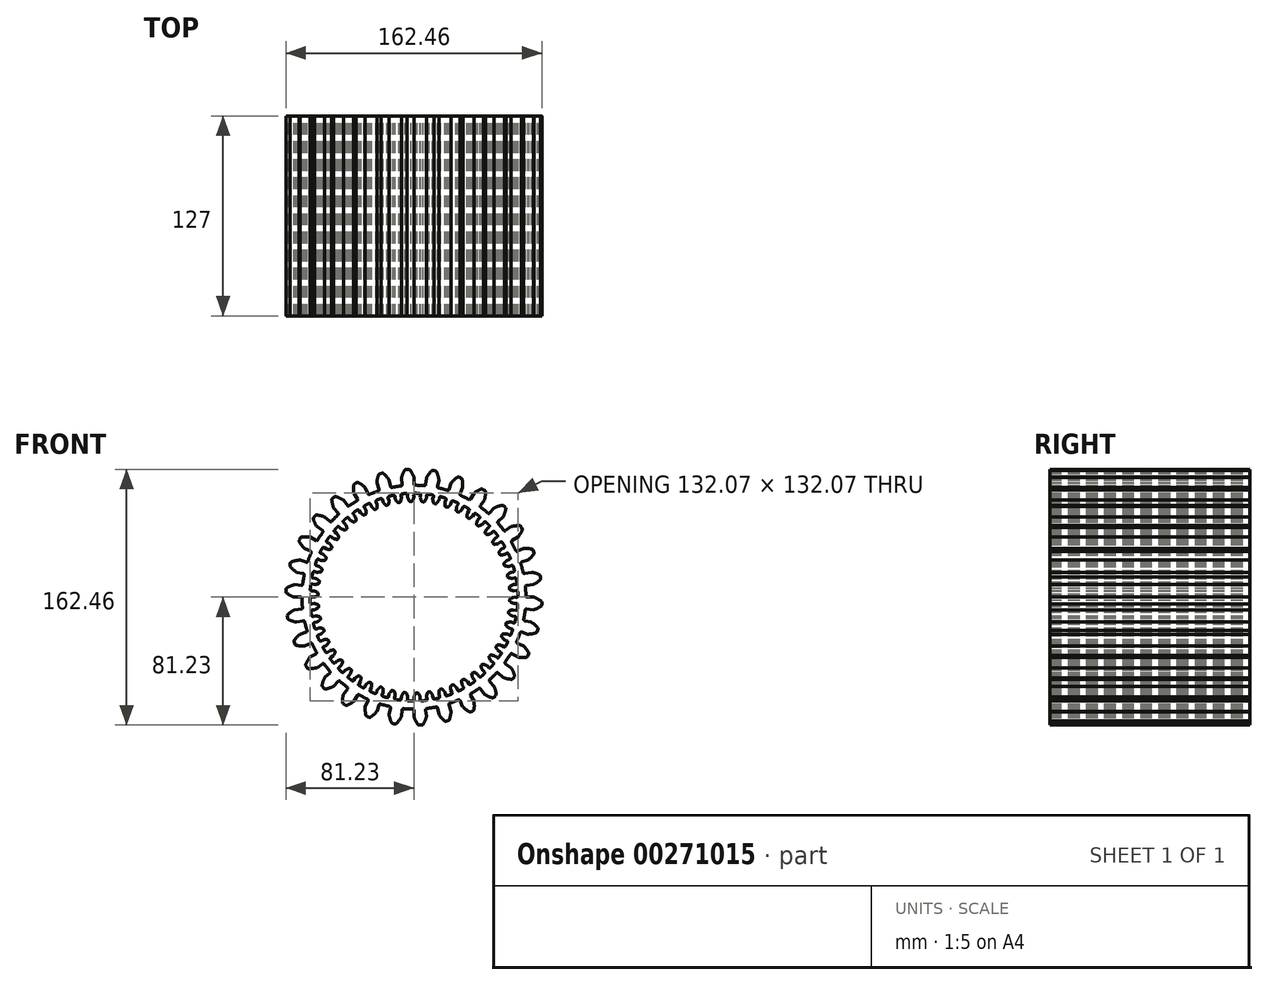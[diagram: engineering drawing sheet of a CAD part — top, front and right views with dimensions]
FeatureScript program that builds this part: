
annotation { "Feature Type Name" : "Feature", "Feature Type Description" : "" }
export const myFeature = defineFeature(function(context is Context, id is Id, definition is map)
    precondition{}
    {
        {
            var Q0;
            Q0=qCreatedBy(makeId("Front.planeOp"),FACE);
            var sketch = newSketch(context, id + "F0", { "sketchPlane" : qUnion([Q0])});
            skArc(sketch, "E0", {"start": v(-8.2, 70.64) * mm, "mid": v(-11.13, 70.24) * mm, "end": v(-14.02, 69.72) * mm});
            skLineSegment(sketch, "E1", {"start": v(-3.26, 81.23) * mm, "end": v(-4.26, 81.23) * mm});
            skLineSegment(sketch, "E2", {"start": v(0, 76.2) * mm, "end": v(0, 71.9) * mm});
            skArc(sketch, "E3.trimOffspring", {"start": v(0, 76.2) * mm, "mid": v(-1.15, 78.65) * mm, "end": v(-2.64, 80.92) * mm});
            skLineSegment(sketch, "E4.MirrorCS", {"start": v(-5.25, 81.13) * mm, "end": v(-4.26, 81.23) * mm});
            skArc(sketch, "E5.MirrorCS", {"start": v(-7.97, 75.78) * mm, "mid": v(-7.08, 78.34) * mm, "end": v(-5.84, 80.75) * mm});
            skLineSegment(sketch, "E6.MirrorCS", {"start": v(-7.97, 75.78) * mm, "end": v(-7.52, 71.5) * mm});
            skPoint(sketch, "E7.visualSharp", {"position": v(-5.63, 81.08) * mm});
            skArc(sketch, "E7.filletArc", {"start": v(-5.25, 81.13) * mm, "mid": v(-5.58, 81) * mm, "end": v(-5.84, 80.75) * mm});
            skPoint(sketch, "E8.visualSharp", {"position": v(-2.88, 81.23) * mm});
            skArc(sketch, "E8.filletArc", {"start": v(-2.64, 80.92) * mm, "mid": v(-2.91, 81.15) * mm, "end": v(-3.26, 81.23) * mm});
            skPoint(sketch, "E9.visualSharp", {"position": v(-7.43, 70.73) * mm});
            skArc(sketch, "E9.filletArc", {"start": v(-8.2, 70.64) * mm, "mid": v(-7.68, 70.93) * mm, "end": v(-7.52, 71.5) * mm});
            skPoint(sketch, "E10.visualSharp", {"position": v(0, 71.12) * mm});
            skArc(sketch, "E10.filletArc", {"start": v(0, 71.9) * mm, "mid": v(0.23, 71.35) * mm, "end": v(0.78, 71.12) * mm});
            skLineSegment(sketch, "E11.1.0", {"start": v(-22, 78.26) * mm, "end": v(-21.05, 78.57) * mm});
            skArc(sketch, "E11.1.1", {"start": v(-22, 78.26) * mm, "mid": v(-22.3, 78.08) * mm, "end": v(-22.5, 77.77) * mm});
            skArc(sketch, "E11.1.2", {"start": v(-23.55, 72.47) * mm, "mid": v(-23.21, 75.16) * mm, "end": v(-22.5, 77.77) * mm});
            skLineSegment(sketch, "E11.1.3", {"start": v(-23.55, 72.47) * mm, "end": v(-22.22, 68.38) * mm});
            skArc(sketch, "E11.1.4", {"start": v(-22.72, 67.4) * mm, "mid": v(-22.26, 67.79) * mm, "end": v(-22.22, 68.38) * mm});
            skLineSegment(sketch, "E11.1.5", {"start": v(-20.08, 78.78) * mm, "end": v(-21.05, 78.57) * mm});
            skArc(sketch, "E11.1.6", {"start": v(-19.4, 78.6) * mm, "mid": v(-19.72, 78.77) * mm, "end": v(-20.08, 78.78) * mm});
            skArc(sketch, "E11.1.7", {"start": v(-15.84, 74.53) * mm, "mid": v(-17.48, 76.7) * mm, "end": v(-19.4, 78.6) * mm});
            skLineSegment(sketch, "E11.1.8", {"start": v(-15.84, 74.53) * mm, "end": v(-14.95, 70.33) * mm});
            skArc(sketch, "E11.1.9", {"start": v(-14.95, 70.33) * mm, "mid": v(-14.61, 69.84) * mm, "end": v(-14.02, 69.72) * mm});
            skLineSegment(sketch, "E11.2.0", {"start": v(-37.79, 71.98) * mm, "end": v(-36.93, 72.47) * mm});
            skArc(sketch, "E11.2.1", {"start": v(-37.79, 71.98) * mm, "mid": v(-38.05, 71.73) * mm, "end": v(-38.18, 71.4) * mm});
            skArc(sketch, "E11.2.2", {"start": v(-38.1, 66) * mm, "mid": v(-38.33, 68.7) * mm, "end": v(-38.18, 71.4) * mm});
            skLineSegment(sketch, "E11.2.3", {"start": v(-38.1, 66) * mm, "end": v(-35.95, 62.27) * mm});
            skArc(sketch, "E11.2.4", {"start": v(-36.23, 61.2) * mm, "mid": v(-35.87, 61.68) * mm, "end": v(-35.95, 62.27) * mm});
            skLineSegment(sketch, "E11.2.5", {"start": v(-36.02, 72.88) * mm, "end": v(-36.93, 72.47) * mm});
            skArc(sketch, "E11.2.6", {"start": v(-35.32, 72.85) * mm, "mid": v(-35.67, 72.95) * mm, "end": v(-36.02, 72.88) * mm});
            skArc(sketch, "E11.2.7", {"start": v(-31, 69.61) * mm, "mid": v(-33.04, 71.39) * mm, "end": v(-35.32, 72.85) * mm});
            skLineSegment(sketch, "E11.2.8", {"start": v(-31, 69.61) * mm, "end": v(-29.25, 65.69) * mm});
            skArc(sketch, "E11.2.9", {"start": v(-29.25, 65.69) * mm, "mid": v(-28.81, 65.27) * mm, "end": v(-28.21, 65.28) * mm});
            skLineSegment(sketch, "E11.3.0", {"start": v(-51.93, 62.55) * mm, "end": v(-51.19, 63.21) * mm});
            skArc(sketch, "E11.3.1", {"start": v(-51.93, 62.55) * mm, "mid": v(-52.13, 62.25) * mm, "end": v(-52.19, 61.9) * mm});
            skArc(sketch, "E11.3.2", {"start": v(-50.99, 56.63) * mm, "mid": v(-51.77, 59.22) * mm, "end": v(-52.19, 61.9) * mm});
            skLineSegment(sketch, "E11.3.3", {"start": v(-50.99, 56.63) * mm, "end": v(-48.11, 53.43) * mm});
            skArc(sketch, "E11.3.4", {"start": v(-48.16, 52.33) * mm, "mid": v(-47.91, 52.87) * mm, "end": v(-48.11, 53.43) * mm});
            skLineSegment(sketch, "E11.3.5", {"start": v(-50.38, 63.8) * mm, "end": v(-51.19, 63.21) * mm});
            skArc(sketch, "E11.3.6", {"start": v(-49.7, 63.92) * mm, "mid": v(-50.05, 63.94) * mm, "end": v(-50.38, 63.8) * mm});
            skArc(sketch, "E11.3.7", {"start": v(-44.79, 61.65) * mm, "mid": v(-47.16, 62.96) * mm, "end": v(-49.7, 63.92) * mm});
            skLineSegment(sketch, "E11.3.8", {"start": v(-44.79, 61.65) * mm, "end": v(-42.26, 58.17) * mm});
            skArc(sketch, "E11.3.9", {"start": v(-42.26, 58.17) * mm, "mid": v(-41.75, 57.86) * mm, "end": v(-41.17, 58) * mm});
            skLineSegment(sketch, "E11.4.0", {"start": v(-63.8, 50.38) * mm, "end": v(-63.21, 51.19) * mm});
            skArc(sketch, "E11.4.1", {"start": v(-63.8, 50.38) * mm, "mid": v(-63.94, 50.05) * mm, "end": v(-63.92, 49.7) * mm});
            skArc(sketch, "E11.4.2", {"start": v(-61.65, 44.79) * mm, "mid": v(-62.96, 47.16) * mm, "end": v(-63.92, 49.7) * mm});
            skLineSegment(sketch, "E11.4.3", {"start": v(-61.65, 44.79) * mm, "end": v(-58.17, 42.26) * mm});
            skArc(sketch, "E11.4.4", {"start": v(-58, 41.17) * mm, "mid": v(-57.86, 41.75) * mm, "end": v(-58.17, 42.26) * mm});
            skLineSegment(sketch, "E11.4.5", {"start": v(-62.55, 51.93) * mm, "end": v(-63.21, 51.19) * mm});
            skArc(sketch, "E11.4.6", {"start": v(-61.9, 52.19) * mm, "mid": v(-62.25, 52.13) * mm, "end": v(-62.55, 51.93) * mm});
            skArc(sketch, "E11.4.7", {"start": v(-56.63, 50.99) * mm, "mid": v(-59.22, 51.77) * mm, "end": v(-61.9, 52.19) * mm});
            skLineSegment(sketch, "E11.4.8", {"start": v(-56.63, 50.99) * mm, "end": v(-53.43, 48.11) * mm});
            skArc(sketch, "E11.4.9", {"start": v(-53.43, 48.11) * mm, "mid": v(-52.87, 47.91) * mm, "end": v(-52.33, 48.16) * mm});
            skLineSegment(sketch, "E11.5.0", {"start": v(-72.88, 36.02) * mm, "end": v(-72.47, 36.93) * mm});
            skArc(sketch, "E11.5.1", {"start": v(-72.88, 36.02) * mm, "mid": v(-72.95, 35.67) * mm, "end": v(-72.85, 35.32) * mm});
            skArc(sketch, "E11.5.2", {"start": v(-69.61, 31) * mm, "mid": v(-71.39, 33.04) * mm, "end": v(-72.85, 35.32) * mm});
            skLineSegment(sketch, "E11.5.3", {"start": v(-69.61, 31) * mm, "end": v(-65.69, 29.25) * mm});
            skArc(sketch, "E11.5.4", {"start": v(-65.28, 28.21) * mm, "mid": v(-65.27, 28.81) * mm, "end": v(-65.69, 29.25) * mm});
            skLineSegment(sketch, "E11.5.5", {"start": v(-71.98, 37.79) * mm, "end": v(-72.47, 36.93) * mm});
            skArc(sketch, "E11.5.6", {"start": v(-71.4, 38.18) * mm, "mid": v(-71.73, 38.05) * mm, "end": v(-71.98, 37.79) * mm});
            skArc(sketch, "E11.5.7", {"start": v(-66, 38.1) * mm, "mid": v(-68.7, 38.33) * mm, "end": v(-71.4, 38.18) * mm});
            skLineSegment(sketch, "E11.5.8", {"start": v(-66, 38.1) * mm, "end": v(-62.27, 35.95) * mm});
            skArc(sketch, "E11.5.9", {"start": v(-62.27, 35.95) * mm, "mid": v(-61.68, 35.87) * mm, "end": v(-61.2, 36.23) * mm});
            skLineSegment(sketch, "E11.6.0", {"start": v(-78.78, 20.08) * mm, "end": v(-78.57, 21.05) * mm});
            skArc(sketch, "E11.6.1", {"start": v(-78.78, 20.08) * mm, "mid": v(-78.77, 19.72) * mm, "end": v(-78.6, 19.4) * mm});
            skArc(sketch, "E11.6.2", {"start": v(-74.53, 15.84) * mm, "mid": v(-76.7, 17.48) * mm, "end": v(-78.6, 19.4) * mm});
            skLineSegment(sketch, "E11.6.3", {"start": v(-74.53, 15.84) * mm, "end": v(-70.33, 14.95) * mm});
            skArc(sketch, "E11.6.4", {"start": v(-69.72, 14.02) * mm, "mid": v(-69.84, 14.61) * mm, "end": v(-70.33, 14.95) * mm});
            skLineSegment(sketch, "E11.6.5", {"start": v(-78.26, 22) * mm, "end": v(-78.57, 21.05) * mm});
            skArc(sketch, "E11.6.6", {"start": v(-77.77, 22.5) * mm, "mid": v(-78.08, 22.3) * mm, "end": v(-78.26, 22) * mm});
            skArc(sketch, "E11.6.7", {"start": v(-72.47, 23.55) * mm, "mid": v(-75.16, 23.21) * mm, "end": v(-77.77, 22.5) * mm});
            skLineSegment(sketch, "E11.6.8", {"start": v(-72.47, 23.55) * mm, "end": v(-68.38, 22.22) * mm});
            skArc(sketch, "E11.6.9", {"start": v(-68.38, 22.22) * mm, "mid": v(-67.79, 22.26) * mm, "end": v(-67.4, 22.72) * mm});
            skLineSegment(sketch, "E11.7.0", {"start": v(-81.23, 3.26) * mm, "end": v(-81.23, 4.26) * mm});
            skArc(sketch, "E11.7.1", {"start": v(-81.23, 3.26) * mm, "mid": v(-81.15, 2.91) * mm, "end": v(-80.92, 2.64) * mm});
            skArc(sketch, "E11.7.2", {"start": v(-76.2, 0) * mm, "mid": v(-78.65, 1.15) * mm, "end": v(-80.92, 2.64) * mm});
            skLineSegment(sketch, "E11.7.3", {"start": v(-76.2, 0) * mm, "end": v(-71.9, 0) * mm});
            skArc(sketch, "E11.7.4", {"start": v(-71.12, -0.78) * mm, "mid": v(-71.35, -0.23) * mm, "end": v(-71.9, 0) * mm});
            skLineSegment(sketch, "E11.7.5", {"start": v(-81.13, 5.25) * mm, "end": v(-81.23, 4.26) * mm});
            skArc(sketch, "E11.7.6", {"start": v(-80.75, 5.84) * mm, "mid": v(-81, 5.58) * mm, "end": v(-81.13, 5.25) * mm});
            skArc(sketch, "E11.7.7", {"start": v(-75.78, 7.97) * mm, "mid": v(-78.34, 7.08) * mm, "end": v(-80.75, 5.84) * mm});
            skLineSegment(sketch, "E11.7.8", {"start": v(-75.78, 7.97) * mm, "end": v(-71.5, 7.52) * mm});
            skArc(sketch, "E11.7.9", {"start": v(-71.5, 7.52) * mm, "mid": v(-70.93, 7.68) * mm, "end": v(-70.64, 8.2) * mm});
            skLineSegment(sketch, "E11.8.0", {"start": v(-80.13, -13.7) * mm, "end": v(-80.34, -12.72) * mm});
            skArc(sketch, "E11.8.1", {"start": v(-80.13, -13.7) * mm, "mid": v(-79.98, -14.02) * mm, "end": v(-79.7, -14.24) * mm});
            skArc(sketch, "E11.8.2", {"start": v(-74.53, -15.84) * mm, "mid": v(-77.17, -15.23) * mm, "end": v(-79.7, -14.24) * mm});
            skLineSegment(sketch, "E11.8.3", {"start": v(-74.53, -15.84) * mm, "end": v(-70.33, -14.95) * mm});
            skArc(sketch, "E11.8.4", {"start": v(-69.4, -15.55) * mm, "mid": v(-69.74, -15.06) * mm, "end": v(-70.33, -14.95) * mm});
            skLineSegment(sketch, "E11.8.5", {"start": v(-80.44, -11.74) * mm, "end": v(-80.34, -12.72) * mm});
            skArc(sketch, "E11.8.6", {"start": v(-80.2, -11.08) * mm, "mid": v(-80.4, -11.38) * mm, "end": v(-80.44, -11.74) * mm});
            skArc(sketch, "E11.8.7", {"start": v(-75.78, -7.97) * mm, "mid": v(-78.1, -9.37) * mm, "end": v(-80.2, -11.08) * mm});
            skLineSegment(sketch, "E11.8.8", {"start": v(-75.78, -7.97) * mm, "end": v(-71.5, -7.52) * mm});
            skArc(sketch, "E11.8.9", {"start": v(-71.5, -7.52) * mm, "mid": v(-70.98, -7.23) * mm, "end": v(-70.8, -6.66) * mm});
            skLineSegment(sketch, "E11.9.0", {"start": v(-75.53, -30.06) * mm, "end": v(-75.94, -29.15) * mm});
            skArc(sketch, "E11.9.1", {"start": v(-75.53, -30.06) * mm, "mid": v(-75.32, -30.34) * mm, "end": v(-75, -30.5) * mm});
            skArc(sketch, "E11.9.2", {"start": v(-69.61, -31) * mm, "mid": v(-72.32, -30.94) * mm, "end": v(-75, -30.5) * mm});
            skLineSegment(sketch, "E11.9.3", {"start": v(-69.61, -31) * mm, "end": v(-65.69, -29.25) * mm});
            skArc(sketch, "E11.9.4", {"start": v(-64.65, -29.64) * mm, "mid": v(-65.09, -29.23) * mm, "end": v(-65.69, -29.25) * mm});
            skLineSegment(sketch, "E11.9.5", {"start": v(-76.25, -28.2) * mm, "end": v(-75.94, -29.15) * mm});
            skArc(sketch, "E11.9.6", {"start": v(-76.14, -27.51) * mm, "mid": v(-76.28, -27.85) * mm, "end": v(-76.25, -28.2) * mm});
            skArc(sketch, "E11.9.7", {"start": v(-72.47, -23.55) * mm, "mid": v(-74.45, -25.4) * mm, "end": v(-76.14, -27.51) * mm});
            skLineSegment(sketch, "E11.9.8", {"start": v(-72.47, -23.55) * mm, "end": v(-68.38, -22.22) * mm});
            skArc(sketch, "E11.9.9", {"start": v(-68.38, -22.22) * mm, "mid": v(-67.93, -21.83) * mm, "end": v(-67.88, -21.24) * mm});
            skLineSegment(sketch, "E11.10.0", {"start": v(-67.63, -45.1) * mm, "end": v(-68.22, -44.3) * mm});
            skArc(sketch, "E11.10.1", {"start": v(-67.63, -45.1) * mm, "mid": v(-67.36, -45.34) * mm, "end": v(-67.01, -45.43) * mm});
            skArc(sketch, "E11.10.2", {"start": v(-61.65, -44.79) * mm, "mid": v(-64.3, -45.3) * mm, "end": v(-67.01, -45.43) * mm});
            skLineSegment(sketch, "E11.10.3", {"start": v(-61.65, -44.79) * mm, "end": v(-58.17, -42.26) * mm});
            skArc(sketch, "E11.10.4", {"start": v(-57.08, -42.43) * mm, "mid": v(-57.59, -42.12) * mm, "end": v(-58.17, -42.26) * mm});
            skLineSegment(sketch, "E11.10.5", {"start": v(-68.72, -43.44) * mm, "end": v(-68.22, -44.3) * mm});
            skArc(sketch, "E11.10.6", {"start": v(-68.76, -42.74) * mm, "mid": v(-68.82, -43.1) * mm, "end": v(-68.72, -43.44) * mm});
            skArc(sketch, "E11.10.7", {"start": v(-66, -38.1) * mm, "mid": v(-67.54, -40.32) * mm, "end": v(-68.76, -42.74) * mm});
            skLineSegment(sketch, "E11.10.8", {"start": v(-66, -38.1) * mm, "end": v(-62.27, -35.95) * mm});
            skArc(sketch, "E11.10.9", {"start": v(-62.27, -35.95) * mm, "mid": v(-61.9, -35.48) * mm, "end": v(-61.98, -34.88) * mm});
            skLineSegment(sketch, "E11.11.0", {"start": v(-56.78, -58.18) * mm, "end": v(-57.52, -57.52) * mm});
            skArc(sketch, "E11.11.1", {"start": v(-56.78, -58.18) * mm, "mid": v(-56.46, -58.35) * mm, "end": v(-56.1, -58.37) * mm});
            skArc(sketch, "E11.11.2", {"start": v(-50.99, -56.63) * mm, "mid": v(-53.48, -57.68) * mm, "end": v(-56.1, -58.37) * mm});
            skLineSegment(sketch, "E11.11.3", {"start": v(-50.99, -56.63) * mm, "end": v(-48.11, -53.43) * mm});
            skArc(sketch, "E11.11.4", {"start": v(-47, -53.37) * mm, "mid": v(-47.57, -53.18) * mm, "end": v(-48.11, -53.43) * mm});
            skLineSegment(sketch, "E11.11.5", {"start": v(-58.18, -56.78) * mm, "end": v(-57.52, -57.52) * mm});
            skArc(sketch, "E11.11.6", {"start": v(-58.37, -56.1) * mm, "mid": v(-58.35, -56.46) * mm, "end": v(-58.18, -56.78) * mm});
            skArc(sketch, "E11.11.7", {"start": v(-56.63, -50.99) * mm, "mid": v(-57.68, -53.48) * mm, "end": v(-58.37, -56.1) * mm});
            skLineSegment(sketch, "E11.11.8", {"start": v(-56.63, -50.99) * mm, "end": v(-53.43, -48.11) * mm});
            skArc(sketch, "E11.11.9", {"start": v(-53.43, -48.11) * mm, "mid": v(-53.18, -47.57) * mm, "end": v(-53.37, -47) * mm});
            skLineSegment(sketch, "E11.12.0", {"start": v(-43.44, -68.72) * mm, "end": v(-44.3, -68.22) * mm});
            skArc(sketch, "E11.12.1", {"start": v(-43.44, -68.72) * mm, "mid": v(-43.1, -68.82) * mm, "end": v(-42.74, -68.76) * mm});
            skArc(sketch, "E11.12.2", {"start": v(-38.1, -66) * mm, "mid": v(-40.32, -67.54) * mm, "end": v(-42.74, -68.76) * mm});
            skLineSegment(sketch, "E11.12.3", {"start": v(-38.1, -66) * mm, "end": v(-35.95, -62.27) * mm});
            skArc(sketch, "E11.12.4", {"start": v(-34.88, -61.98) * mm, "mid": v(-35.48, -61.9) * mm, "end": v(-35.95, -62.27) * mm});
            skLineSegment(sketch, "E11.12.5", {"start": v(-45.1, -67.63) * mm, "end": v(-44.3, -68.22) * mm});
            skArc(sketch, "E11.12.6", {"start": v(-45.43, -67.01) * mm, "mid": v(-45.34, -67.36) * mm, "end": v(-45.1, -67.63) * mm});
            skArc(sketch, "E11.12.7", {"start": v(-44.79, -61.65) * mm, "mid": v(-45.3, -64.3) * mm, "end": v(-45.43, -67.01) * mm});
            skLineSegment(sketch, "E11.12.8", {"start": v(-44.79, -61.65) * mm, "end": v(-42.26, -58.17) * mm});
            skArc(sketch, "E11.12.9", {"start": v(-42.26, -58.17) * mm, "mid": v(-42.12, -57.59) * mm, "end": v(-42.43, -57.08) * mm});
            skLineSegment(sketch, "E11.13.0", {"start": v(-28.2, -76.25) * mm, "end": v(-29.15, -75.94) * mm});
            skArc(sketch, "E11.13.1", {"start": v(-28.2, -76.25) * mm, "mid": v(-27.85, -76.28) * mm, "end": v(-27.51, -76.14) * mm});
            skArc(sketch, "E11.13.2", {"start": v(-23.55, -72.47) * mm, "mid": v(-25.4, -74.45) * mm, "end": v(-27.51, -76.14) * mm});
            skLineSegment(sketch, "E11.13.3", {"start": v(-23.55, -72.47) * mm, "end": v(-22.22, -68.38) * mm});
            skArc(sketch, "E11.13.4", {"start": v(-21.24, -67.88) * mm, "mid": v(-21.83, -67.93) * mm, "end": v(-22.22, -68.38) * mm});
            skLineSegment(sketch, "E11.13.5", {"start": v(-30.06, -75.53) * mm, "end": v(-29.15, -75.94) * mm});
            skArc(sketch, "E11.13.6", {"start": v(-30.5, -75) * mm, "mid": v(-30.34, -75.32) * mm, "end": v(-30.06, -75.53) * mm});
            skArc(sketch, "E11.13.7", {"start": v(-31, -69.61) * mm, "mid": v(-30.94, -72.32) * mm, "end": v(-30.5, -75) * mm});
            skLineSegment(sketch, "E11.13.8", {"start": v(-31, -69.61) * mm, "end": v(-29.25, -65.69) * mm});
            skArc(sketch, "E11.13.9", {"start": v(-29.25, -65.69) * mm, "mid": v(-29.23, -65.09) * mm, "end": v(-29.64, -64.65) * mm});
            skLineSegment(sketch, "E11.14.0", {"start": v(-11.74, -80.44) * mm, "end": v(-12.72, -80.34) * mm});
            skArc(sketch, "E11.14.1", {"start": v(-11.74, -80.44) * mm, "mid": v(-11.38, -80.4) * mm, "end": v(-11.08, -80.2) * mm});
            skArc(sketch, "E11.14.2", {"start": v(-7.97, -75.78) * mm, "mid": v(-9.37, -78.1) * mm, "end": v(-11.08, -80.2) * mm});
            skLineSegment(sketch, "E11.14.3", {"start": v(-7.97, -75.78) * mm, "end": v(-7.52, -71.5) * mm});
            skArc(sketch, "E11.14.4", {"start": v(-6.66, -70.8) * mm, "mid": v(-7.23, -70.98) * mm, "end": v(-7.52, -71.5) * mm});
            skLineSegment(sketch, "E11.14.5", {"start": v(-13.7, -80.13) * mm, "end": v(-12.72, -80.34) * mm});
            skArc(sketch, "E11.14.6", {"start": v(-14.24, -79.7) * mm, "mid": v(-14.02, -79.98) * mm, "end": v(-13.7, -80.13) * mm});
            skArc(sketch, "E11.14.7", {"start": v(-15.84, -74.53) * mm, "mid": v(-15.23, -77.17) * mm, "end": v(-14.24, -79.7) * mm});
            skLineSegment(sketch, "E11.14.8", {"start": v(-15.84, -74.53) * mm, "end": v(-14.95, -70.33) * mm});
            skArc(sketch, "E11.14.9", {"start": v(-14.95, -70.33) * mm, "mid": v(-15.06, -69.74) * mm, "end": v(-15.55, -69.4) * mm});
            skLineSegment(sketch, "E11.15.0", {"start": v(5.25, -81.13) * mm, "end": v(4.26, -81.23) * mm});
            skArc(sketch, "E11.15.1", {"start": v(5.25, -81.13) * mm, "mid": v(5.58, -81) * mm, "end": v(5.84, -80.75) * mm});
            skArc(sketch, "E11.15.2", {"start": v(7.97, -75.78) * mm, "mid": v(7.08, -78.34) * mm, "end": v(5.84, -80.75) * mm});
            skLineSegment(sketch, "E11.15.3", {"start": v(7.97, -75.78) * mm, "end": v(7.52, -71.5) * mm});
            skArc(sketch, "E11.15.4", {"start": v(8.2, -70.64) * mm, "mid": v(7.68, -70.93) * mm, "end": v(7.52, -71.5) * mm});
            skLineSegment(sketch, "E11.15.5", {"start": v(3.26, -81.23) * mm, "end": v(4.26, -81.23) * mm});
            skArc(sketch, "E11.15.6", {"start": v(2.64, -80.92) * mm, "mid": v(2.91, -81.15) * mm, "end": v(3.26, -81.23) * mm});
            skArc(sketch, "E11.15.7", {"start": v(0, -76.2) * mm, "mid": v(1.15, -78.65) * mm, "end": v(2.64, -80.92) * mm});
            skLineSegment(sketch, "E11.15.8", {"start": v(0, -76.2) * mm, "end": v(0, -71.9) * mm});
            skArc(sketch, "E11.15.9", {"start": v(0, -71.9) * mm, "mid": v(-0.23, -71.35) * mm, "end": v(-0.78, -71.12) * mm});
            skLineSegment(sketch, "E11.16.0", {"start": v(22, -78.26) * mm, "end": v(21.05, -78.57) * mm});
            skArc(sketch, "E11.16.1", {"start": v(22, -78.26) * mm, "mid": v(22.3, -78.08) * mm, "end": v(22.5, -77.77) * mm});
            skArc(sketch, "E11.16.2", {"start": v(23.55, -72.47) * mm, "mid": v(23.21, -75.16) * mm, "end": v(22.5, -77.77) * mm});
            skLineSegment(sketch, "E11.16.3", {"start": v(23.55, -72.47) * mm, "end": v(22.22, -68.38) * mm});
            skArc(sketch, "E11.16.4", {"start": v(22.72, -67.4) * mm, "mid": v(22.26, -67.79) * mm, "end": v(22.22, -68.38) * mm});
            skLineSegment(sketch, "E11.16.5", {"start": v(20.08, -78.78) * mm, "end": v(21.05, -78.57) * mm});
            skArc(sketch, "E11.16.6", {"start": v(19.4, -78.6) * mm, "mid": v(19.72, -78.77) * mm, "end": v(20.08, -78.78) * mm});
            skArc(sketch, "E11.16.7", {"start": v(15.84, -74.53) * mm, "mid": v(17.48, -76.7) * mm, "end": v(19.4, -78.6) * mm});
            skLineSegment(sketch, "E11.16.8", {"start": v(15.84, -74.53) * mm, "end": v(14.95, -70.33) * mm});
            skArc(sketch, "E11.16.9", {"start": v(14.95, -70.33) * mm, "mid": v(14.61, -69.84) * mm, "end": v(14.02, -69.72) * mm});
            skLineSegment(sketch, "E11.17.0", {"start": v(37.79, -71.98) * mm, "end": v(36.93, -72.47) * mm});
            skArc(sketch, "E11.17.1", {"start": v(37.79, -71.98) * mm, "mid": v(38.05, -71.73) * mm, "end": v(38.18, -71.4) * mm});
            skArc(sketch, "E11.17.2", {"start": v(38.1, -66) * mm, "mid": v(38.33, -68.7) * mm, "end": v(38.18, -71.4) * mm});
            skLineSegment(sketch, "E11.17.3", {"start": v(38.1, -66) * mm, "end": v(35.95, -62.27) * mm});
            skArc(sketch, "E11.17.4", {"start": v(36.23, -61.2) * mm, "mid": v(35.87, -61.68) * mm, "end": v(35.95, -62.27) * mm});
            skLineSegment(sketch, "E11.17.5", {"start": v(36.02, -72.88) * mm, "end": v(36.93, -72.47) * mm});
            skArc(sketch, "E11.17.6", {"start": v(35.32, -72.85) * mm, "mid": v(35.67, -72.95) * mm, "end": v(36.02, -72.88) * mm});
            skArc(sketch, "E11.17.7", {"start": v(31, -69.61) * mm, "mid": v(33.04, -71.39) * mm, "end": v(35.32, -72.85) * mm});
            skLineSegment(sketch, "E11.17.8", {"start": v(31, -69.61) * mm, "end": v(29.25, -65.69) * mm});
            skArc(sketch, "E11.17.9", {"start": v(29.25, -65.69) * mm, "mid": v(28.81, -65.27) * mm, "end": v(28.21, -65.28) * mm});
            skLineSegment(sketch, "E11.18.0", {"start": v(51.93, -62.55) * mm, "end": v(51.19, -63.21) * mm});
            skArc(sketch, "E11.18.1", {"start": v(51.93, -62.55) * mm, "mid": v(52.13, -62.25) * mm, "end": v(52.19, -61.9) * mm});
            skArc(sketch, "E11.18.2", {"start": v(50.99, -56.63) * mm, "mid": v(51.77, -59.22) * mm, "end": v(52.19, -61.9) * mm});
            skLineSegment(sketch, "E11.18.3", {"start": v(50.99, -56.63) * mm, "end": v(48.11, -53.43) * mm});
            skArc(sketch, "E11.18.4", {"start": v(48.16, -52.33) * mm, "mid": v(47.91, -52.87) * mm, "end": v(48.11, -53.43) * mm});
            skLineSegment(sketch, "E11.18.5", {"start": v(50.38, -63.8) * mm, "end": v(51.19, -63.21) * mm});
            skArc(sketch, "E11.18.6", {"start": v(49.7, -63.92) * mm, "mid": v(50.05, -63.94) * mm, "end": v(50.38, -63.8) * mm});
            skArc(sketch, "E11.18.7", {"start": v(44.79, -61.65) * mm, "mid": v(47.16, -62.96) * mm, "end": v(49.7, -63.92) * mm});
            skLineSegment(sketch, "E11.18.8", {"start": v(44.79, -61.65) * mm, "end": v(42.26, -58.17) * mm});
            skArc(sketch, "E11.18.9", {"start": v(42.26, -58.17) * mm, "mid": v(41.75, -57.86) * mm, "end": v(41.17, -58) * mm});
            skLineSegment(sketch, "E11.19.0", {"start": v(63.8, -50.38) * mm, "end": v(63.21, -51.19) * mm});
            skArc(sketch, "E11.19.1", {"start": v(63.8, -50.38) * mm, "mid": v(63.94, -50.05) * mm, "end": v(63.92, -49.7) * mm});
            skArc(sketch, "E11.19.2", {"start": v(61.65, -44.79) * mm, "mid": v(62.96, -47.16) * mm, "end": v(63.92, -49.7) * mm});
            skLineSegment(sketch, "E11.19.3", {"start": v(61.65, -44.79) * mm, "end": v(58.17, -42.26) * mm});
            skArc(sketch, "E11.19.4", {"start": v(58, -41.17) * mm, "mid": v(57.86, -41.75) * mm, "end": v(58.17, -42.26) * mm});
            skLineSegment(sketch, "E11.19.5", {"start": v(62.55, -51.93) * mm, "end": v(63.21, -51.19) * mm});
            skArc(sketch, "E11.19.6", {"start": v(61.9, -52.19) * mm, "mid": v(62.25, -52.13) * mm, "end": v(62.55, -51.93) * mm});
            skArc(sketch, "E11.19.7", {"start": v(56.63, -50.99) * mm, "mid": v(59.22, -51.77) * mm, "end": v(61.9, -52.19) * mm});
            skLineSegment(sketch, "E11.19.8", {"start": v(56.63, -50.99) * mm, "end": v(53.43, -48.11) * mm});
            skArc(sketch, "E11.19.9", {"start": v(53.43, -48.11) * mm, "mid": v(52.87, -47.91) * mm, "end": v(52.33, -48.16) * mm});
            skLineSegment(sketch, "E11.20.0", {"start": v(72.88, -36.02) * mm, "end": v(72.47, -36.93) * mm});
            skArc(sketch, "E11.20.1", {"start": v(72.88, -36.02) * mm, "mid": v(72.95, -35.67) * mm, "end": v(72.85, -35.32) * mm});
            skArc(sketch, "E11.20.2", {"start": v(69.61, -31) * mm, "mid": v(71.39, -33.04) * mm, "end": v(72.85, -35.32) * mm});
            skLineSegment(sketch, "E11.20.3", {"start": v(69.61, -31) * mm, "end": v(65.69, -29.25) * mm});
            skArc(sketch, "E11.20.4", {"start": v(65.28, -28.21) * mm, "mid": v(65.27, -28.81) * mm, "end": v(65.69, -29.25) * mm});
            skLineSegment(sketch, "E11.20.5", {"start": v(71.98, -37.79) * mm, "end": v(72.47, -36.93) * mm});
            skArc(sketch, "E11.20.6", {"start": v(71.4, -38.18) * mm, "mid": v(71.73, -38.05) * mm, "end": v(71.98, -37.79) * mm});
            skArc(sketch, "E11.20.7", {"start": v(66, -38.1) * mm, "mid": v(68.7, -38.33) * mm, "end": v(71.4, -38.18) * mm});
            skLineSegment(sketch, "E11.20.8", {"start": v(66, -38.1) * mm, "end": v(62.27, -35.95) * mm});
            skArc(sketch, "E11.20.9", {"start": v(62.27, -35.95) * mm, "mid": v(61.68, -35.87) * mm, "end": v(61.2, -36.23) * mm});
            skLineSegment(sketch, "E11.21.0", {"start": v(78.78, -20.08) * mm, "end": v(78.57, -21.05) * mm});
            skArc(sketch, "E11.21.1", {"start": v(78.78, -20.08) * mm, "mid": v(78.77, -19.72) * mm, "end": v(78.6, -19.4) * mm});
            skArc(sketch, "E11.21.2", {"start": v(74.53, -15.84) * mm, "mid": v(76.7, -17.48) * mm, "end": v(78.6, -19.4) * mm});
            skLineSegment(sketch, "E11.21.3", {"start": v(74.53, -15.84) * mm, "end": v(70.33, -14.95) * mm});
            skArc(sketch, "E11.21.4", {"start": v(69.72, -14.02) * mm, "mid": v(69.84, -14.61) * mm, "end": v(70.33, -14.95) * mm});
            skLineSegment(sketch, "E11.21.5", {"start": v(78.26, -22) * mm, "end": v(78.57, -21.05) * mm});
            skArc(sketch, "E11.21.6", {"start": v(77.77, -22.5) * mm, "mid": v(78.08, -22.3) * mm, "end": v(78.26, -22) * mm});
            skArc(sketch, "E11.21.7", {"start": v(72.47, -23.55) * mm, "mid": v(75.16, -23.21) * mm, "end": v(77.77, -22.5) * mm});
            skLineSegment(sketch, "E11.21.8", {"start": v(72.47, -23.55) * mm, "end": v(68.38, -22.22) * mm});
            skArc(sketch, "E11.21.9", {"start": v(68.38, -22.22) * mm, "mid": v(67.79, -22.26) * mm, "end": v(67.4, -22.72) * mm});
            skLineSegment(sketch, "E11.22.0", {"start": v(81.23, -3.26) * mm, "end": v(81.23, -4.26) * mm});
            skArc(sketch, "E11.22.1", {"start": v(81.23, -3.26) * mm, "mid": v(81.15, -2.91) * mm, "end": v(80.92, -2.64) * mm});
            skArc(sketch, "E11.22.2", {"start": v(76.2, 0) * mm, "mid": v(78.65, -1.15) * mm, "end": v(80.92, -2.64) * mm});
            skLineSegment(sketch, "E11.22.3", {"start": v(76.2, 0) * mm, "end": v(71.9, 0) * mm});
            skArc(sketch, "E11.22.4", {"start": v(71.12, 0.78) * mm, "mid": v(71.35, 0.23) * mm, "end": v(71.9, 0) * mm});
            skLineSegment(sketch, "E11.22.5", {"start": v(81.13, -5.25) * mm, "end": v(81.23, -4.26) * mm});
            skArc(sketch, "E11.22.6", {"start": v(80.75, -5.84) * mm, "mid": v(81, -5.58) * mm, "end": v(81.13, -5.25) * mm});
            skArc(sketch, "E11.22.7", {"start": v(75.78, -7.97) * mm, "mid": v(78.34, -7.08) * mm, "end": v(80.75, -5.84) * mm});
            skLineSegment(sketch, "E11.22.8", {"start": v(75.78, -7.97) * mm, "end": v(71.5, -7.52) * mm});
            skArc(sketch, "E11.22.9", {"start": v(71.5, -7.52) * mm, "mid": v(70.93, -7.68) * mm, "end": v(70.64, -8.2) * mm});
            skLineSegment(sketch, "E11.23.0", {"start": v(80.13, 13.7) * mm, "end": v(80.34, 12.72) * mm});
            skArc(sketch, "E11.23.1", {"start": v(80.13, 13.7) * mm, "mid": v(79.98, 14.02) * mm, "end": v(79.7, 14.24) * mm});
            skArc(sketch, "E11.23.2", {"start": v(74.53, 15.84) * mm, "mid": v(77.17, 15.23) * mm, "end": v(79.7, 14.24) * mm});
            skLineSegment(sketch, "E11.23.3", {"start": v(74.53, 15.84) * mm, "end": v(70.33, 14.95) * mm});
            skArc(sketch, "E11.23.4", {"start": v(69.4, 15.55) * mm, "mid": v(69.74, 15.06) * mm, "end": v(70.33, 14.95) * mm});
            skLineSegment(sketch, "E11.23.5", {"start": v(80.44, 11.74) * mm, "end": v(80.34, 12.72) * mm});
            skArc(sketch, "E11.23.6", {"start": v(80.2, 11.08) * mm, "mid": v(80.4, 11.38) * mm, "end": v(80.44, 11.74) * mm});
            skArc(sketch, "E11.23.7", {"start": v(75.78, 7.97) * mm, "mid": v(78.1, 9.37) * mm, "end": v(80.2, 11.08) * mm});
            skLineSegment(sketch, "E11.23.8", {"start": v(75.78, 7.97) * mm, "end": v(71.5, 7.52) * mm});
            skArc(sketch, "E11.23.9", {"start": v(71.5, 7.52) * mm, "mid": v(70.98, 7.23) * mm, "end": v(70.8, 6.66) * mm});
            skLineSegment(sketch, "E11.24.0", {"start": v(75.53, 30.06) * mm, "end": v(75.94, 29.15) * mm});
            skArc(sketch, "E11.24.1", {"start": v(75.53, 30.06) * mm, "mid": v(75.32, 30.34) * mm, "end": v(75, 30.5) * mm});
            skArc(sketch, "E11.24.2", {"start": v(69.61, 31) * mm, "mid": v(72.32, 30.94) * mm, "end": v(75, 30.5) * mm});
            skLineSegment(sketch, "E11.24.3", {"start": v(69.61, 31) * mm, "end": v(65.69, 29.25) * mm});
            skArc(sketch, "E11.24.4", {"start": v(64.65, 29.64) * mm, "mid": v(65.09, 29.23) * mm, "end": v(65.69, 29.25) * mm});
            skLineSegment(sketch, "E11.24.5", {"start": v(76.25, 28.2) * mm, "end": v(75.94, 29.15) * mm});
            skArc(sketch, "E11.24.6", {"start": v(76.14, 27.51) * mm, "mid": v(76.28, 27.85) * mm, "end": v(76.25, 28.2) * mm});
            skArc(sketch, "E11.24.7", {"start": v(72.47, 23.55) * mm, "mid": v(74.45, 25.4) * mm, "end": v(76.14, 27.51) * mm});
            skLineSegment(sketch, "E11.24.8", {"start": v(72.47, 23.55) * mm, "end": v(68.38, 22.22) * mm});
            skArc(sketch, "E11.24.9", {"start": v(68.38, 22.22) * mm, "mid": v(67.93, 21.83) * mm, "end": v(67.88, 21.24) * mm});
            skLineSegment(sketch, "E11.25.0", {"start": v(67.63, 45.1) * mm, "end": v(68.22, 44.3) * mm});
            skArc(sketch, "E11.25.1", {"start": v(67.63, 45.1) * mm, "mid": v(67.36, 45.34) * mm, "end": v(67.01, 45.43) * mm});
            skArc(sketch, "E11.25.2", {"start": v(61.65, 44.79) * mm, "mid": v(64.3, 45.3) * mm, "end": v(67.01, 45.43) * mm});
            skLineSegment(sketch, "E11.25.3", {"start": v(61.65, 44.79) * mm, "end": v(58.17, 42.26) * mm});
            skArc(sketch, "E11.25.4", {"start": v(57.08, 42.43) * mm, "mid": v(57.59, 42.12) * mm, "end": v(58.17, 42.26) * mm});
            skLineSegment(sketch, "E11.25.5", {"start": v(68.72, 43.44) * mm, "end": v(68.22, 44.3) * mm});
            skArc(sketch, "E11.25.6", {"start": v(68.76, 42.74) * mm, "mid": v(68.82, 43.1) * mm, "end": v(68.72, 43.44) * mm});
            skArc(sketch, "E11.25.7", {"start": v(66, 38.1) * mm, "mid": v(67.54, 40.32) * mm, "end": v(68.76, 42.74) * mm});
            skLineSegment(sketch, "E11.25.8", {"start": v(66, 38.1) * mm, "end": v(62.27, 35.95) * mm});
            skArc(sketch, "E11.25.9", {"start": v(62.27, 35.95) * mm, "mid": v(61.9, 35.48) * mm, "end": v(61.98, 34.88) * mm});
            skLineSegment(sketch, "E11.26.0", {"start": v(56.78, 58.18) * mm, "end": v(57.52, 57.52) * mm});
            skArc(sketch, "E11.26.1", {"start": v(56.78, 58.18) * mm, "mid": v(56.46, 58.35) * mm, "end": v(56.1, 58.37) * mm});
            skArc(sketch, "E11.26.2", {"start": v(50.99, 56.63) * mm, "mid": v(53.48, 57.68) * mm, "end": v(56.1, 58.37) * mm});
            skLineSegment(sketch, "E11.26.3", {"start": v(50.99, 56.63) * mm, "end": v(48.11, 53.43) * mm});
            skArc(sketch, "E11.26.4", {"start": v(47, 53.37) * mm, "mid": v(47.57, 53.18) * mm, "end": v(48.11, 53.43) * mm});
            skLineSegment(sketch, "E11.26.5", {"start": v(58.18, 56.78) * mm, "end": v(57.52, 57.52) * mm});
            skArc(sketch, "E11.26.6", {"start": v(58.37, 56.1) * mm, "mid": v(58.35, 56.46) * mm, "end": v(58.18, 56.78) * mm});
            skArc(sketch, "E11.26.7", {"start": v(56.63, 50.99) * mm, "mid": v(57.68, 53.48) * mm, "end": v(58.37, 56.1) * mm});
            skLineSegment(sketch, "E11.26.8", {"start": v(56.63, 50.99) * mm, "end": v(53.43, 48.11) * mm});
            skArc(sketch, "E11.26.9", {"start": v(53.43, 48.11) * mm, "mid": v(53.18, 47.57) * mm, "end": v(53.37, 47) * mm});
            skLineSegment(sketch, "E11.27.0", {"start": v(43.44, 68.72) * mm, "end": v(44.3, 68.22) * mm});
            skArc(sketch, "E11.27.1", {"start": v(43.44, 68.72) * mm, "mid": v(43.1, 68.82) * mm, "end": v(42.74, 68.76) * mm});
            skArc(sketch, "E11.27.2", {"start": v(38.1, 66) * mm, "mid": v(40.32, 67.54) * mm, "end": v(42.74, 68.76) * mm});
            skLineSegment(sketch, "E11.27.3", {"start": v(38.1, 66) * mm, "end": v(35.95, 62.27) * mm});
            skArc(sketch, "E11.27.4", {"start": v(34.88, 61.98) * mm, "mid": v(35.48, 61.9) * mm, "end": v(35.95, 62.27) * mm});
            skLineSegment(sketch, "E11.27.5", {"start": v(45.1, 67.63) * mm, "end": v(44.3, 68.22) * mm});
            skArc(sketch, "E11.27.6", {"start": v(45.43, 67.01) * mm, "mid": v(45.34, 67.36) * mm, "end": v(45.1, 67.63) * mm});
            skArc(sketch, "E11.27.7", {"start": v(44.79, 61.65) * mm, "mid": v(45.3, 64.3) * mm, "end": v(45.43, 67.01) * mm});
            skLineSegment(sketch, "E11.27.8", {"start": v(44.79, 61.65) * mm, "end": v(42.26, 58.17) * mm});
            skArc(sketch, "E11.27.9", {"start": v(42.26, 58.17) * mm, "mid": v(42.12, 57.59) * mm, "end": v(42.43, 57.08) * mm});
            skLineSegment(sketch, "E11.28.0", {"start": v(28.2, 76.25) * mm, "end": v(29.15, 75.94) * mm});
            skArc(sketch, "E11.28.1", {"start": v(28.2, 76.25) * mm, "mid": v(27.85, 76.28) * mm, "end": v(27.51, 76.14) * mm});
            skArc(sketch, "E11.28.2", {"start": v(23.55, 72.47) * mm, "mid": v(25.4, 74.45) * mm, "end": v(27.51, 76.14) * mm});
            skLineSegment(sketch, "E11.28.3", {"start": v(23.55, 72.47) * mm, "end": v(22.22, 68.38) * mm});
            skArc(sketch, "E11.28.4", {"start": v(21.24, 67.88) * mm, "mid": v(21.83, 67.93) * mm, "end": v(22.22, 68.38) * mm});
            skLineSegment(sketch, "E11.28.5", {"start": v(30.06, 75.53) * mm, "end": v(29.15, 75.94) * mm});
            skArc(sketch, "E11.28.6", {"start": v(30.5, 75) * mm, "mid": v(30.34, 75.32) * mm, "end": v(30.06, 75.53) * mm});
            skArc(sketch, "E11.28.7", {"start": v(31, 69.61) * mm, "mid": v(30.94, 72.32) * mm, "end": v(30.5, 75) * mm});
            skLineSegment(sketch, "E11.28.8", {"start": v(31, 69.61) * mm, "end": v(29.25, 65.69) * mm});
            skArc(sketch, "E11.28.9", {"start": v(29.25, 65.69) * mm, "mid": v(29.23, 65.09) * mm, "end": v(29.64, 64.65) * mm});
            skLineSegment(sketch, "E11.29.0", {"start": v(11.74, 80.44) * mm, "end": v(12.72, 80.34) * mm});
            skArc(sketch, "E11.29.1", {"start": v(11.74, 80.44) * mm, "mid": v(11.38, 80.4) * mm, "end": v(11.08, 80.2) * mm});
            skArc(sketch, "E11.29.2", {"start": v(7.97, 75.78) * mm, "mid": v(9.37, 78.1) * mm, "end": v(11.08, 80.2) * mm});
            skLineSegment(sketch, "E11.29.3", {"start": v(7.97, 75.78) * mm, "end": v(7.52, 71.5) * mm});
            skArc(sketch, "E11.29.4", {"start": v(6.66, 70.8) * mm, "mid": v(7.23, 70.98) * mm, "end": v(7.52, 71.5) * mm});
            skLineSegment(sketch, "E11.29.5", {"start": v(13.7, 80.13) * mm, "end": v(12.72, 80.34) * mm});
            skArc(sketch, "E11.29.6", {"start": v(14.24, 79.7) * mm, "mid": v(14.02, 79.98) * mm, "end": v(13.7, 80.13) * mm});
            skArc(sketch, "E11.29.7", {"start": v(15.84, 74.53) * mm, "mid": v(15.23, 77.17) * mm, "end": v(14.24, 79.7) * mm});
            skLineSegment(sketch, "E11.29.8", {"start": v(15.84, 74.53) * mm, "end": v(14.95, 70.33) * mm});
            skArc(sketch, "E11.29.9", {"start": v(14.95, 70.33) * mm, "mid": v(15.06, 69.74) * mm, "end": v(15.55, 69.4) * mm});
            skArc(sketch, "E12", {"start": v(-4.83, 65.86) * mm, "mid": v(-6.21, 65.75) * mm, "end": v(-7.6, 65.6) * mm});
            skLineSegment(sketch, "E13", {"start": v(0, 0) * mm, "end": v(-2.82, 89.86) * mm, "construction": true});
            skLineSegment(sketch, "E14.MirrorCS", {"start": v(-3.99, 63.37) * mm, "end": v(-3.99, 65.08) * mm});
            skArc(sketch, "E15.MirrorCS", {"start": v(-3.99, 63.37) * mm, "mid": v(-3.52, 62.3) * mm, "end": v(-2.98, 61.25) * mm});
            skLineSegment(sketch, "E16.MirrorCS", {"start": v(-2.3, 60.85) * mm, "end": v(-1.91, 60.85) * mm});
            skLineSegment(sketch, "E17.MirrorCS", {"start": v(-1.53, 60.87) * mm, "end": v(-1.91, 60.85) * mm});
            skArc(sketch, "E18.MirrorCS", {"start": v(0, 63.5) * mm, "mid": v(-0.4, 62.39) * mm, "end": v(-0.87, 61.31) * mm});
            skLineSegment(sketch, "E19.MirrorCS", {"start": v(0, 63.5) * mm, "end": v(-0.1, 65.2) * mm});
            skPoint(sketch, "E20.visualSharp", {"position": v(-3.99, 65.92) * mm});
            skArc(sketch, "E20.filletArc", {"start": v(-3.99, 65.08) * mm, "mid": v(-4.24, 65.65) * mm, "end": v(-4.83, 65.86) * mm});
            skPoint(sketch, "E21.visualSharp", {"position": v(-0.16, 66.04) * mm});
            skArc(sketch, "E21.filletArc", {"start": v(0.69, 66.04) * mm, "mid": v(0.1, 65.8) * mm, "end": v(-0.1, 65.2) * mm});
            skPoint(sketch, "E22.visualSharp", {"position": v(-2.75, 60.85) * mm});
            skArc(sketch, "E22.filletArc", {"start": v(-2.98, 61.25) * mm, "mid": v(-2.7, 60.95) * mm, "end": v(-2.3, 60.85) * mm});
            skPoint(sketch, "E23.visualSharp", {"position": v(-1.08, 60.9) * mm});
            skArc(sketch, "E23.filletArc", {"start": v(-1.53, 60.87) * mm, "mid": v(-1.14, 61) * mm, "end": v(-0.87, 61.31) * mm});
            skArc(sketch, "E24.1.0", {"start": v(-12.11, 64.06) * mm, "mid": v(-12.43, 64.6) * mm, "end": v(-13.05, 64.74) * mm});
            skLineSegment(sketch, "E24.1.1", {"start": v(-11.9, 62.38) * mm, "end": v(-12.11, 64.06) * mm});
            skArc(sketch, "E24.1.2", {"start": v(-11.9, 62.38) * mm, "mid": v(-11.3, 61.36) * mm, "end": v(-10.63, 60.39) * mm});
            skArc(sketch, "E24.1.3", {"start": v(-10.63, 60.39) * mm, "mid": v(-10.31, 60.14) * mm, "end": v(-9.9, 60.08) * mm});
            skLineSegment(sketch, "E24.1.4", {"start": v(-9.9, 60.08) * mm, "end": v(-9.52, 60.13) * mm});
            skLineSegment(sketch, "E24.1.5", {"start": v(-9.15, 60.2) * mm, "end": v(-9.52, 60.13) * mm});
            skArc(sketch, "E24.1.6", {"start": v(-9.15, 60.2) * mm, "mid": v(-8.78, 60.38) * mm, "end": v(-8.55, 60.72) * mm});
            skArc(sketch, "E24.1.7", {"start": v(-7.96, 63) * mm, "mid": v(-8.21, 61.85) * mm, "end": v(-8.55, 60.72) * mm});
            skLineSegment(sketch, "E24.1.8", {"start": v(-7.96, 63) * mm, "end": v(-8.28, 64.67) * mm});
            skArc(sketch, "E24.1.9", {"start": v(-7.6, 65.6) * mm, "mid": v(-8.14, 65.29) * mm, "end": v(-8.28, 64.67) * mm});
            skArc(sketch, "E24.2.0", {"start": v(-20.05, 62.04) * mm, "mid": v(-20.43, 62.54) * mm, "end": v(-21.06, 62.6) * mm});
            skLineSegment(sketch, "E24.2.1", {"start": v(-19.62, 60.4) * mm, "end": v(-20.05, 62.04) * mm});
            skArc(sketch, "E24.2.2", {"start": v(-19.62, 60.4) * mm, "mid": v(-18.9, 59.46) * mm, "end": v(-18.12, 58.58) * mm});
            skArc(sketch, "E24.2.3", {"start": v(-18.12, 58.58) * mm, "mid": v(-17.77, 58.37) * mm, "end": v(-17.36, 58.36) * mm});
            skLineSegment(sketch, "E24.2.4", {"start": v(-17.36, 58.36) * mm, "end": v(-16.98, 58.46) * mm});
            skLineSegment(sketch, "E24.2.5", {"start": v(-16.62, 58.58) * mm, "end": v(-16.98, 58.46) * mm});
            skArc(sketch, "E24.2.6", {"start": v(-16.62, 58.58) * mm, "mid": v(-16.27, 58.8) * mm, "end": v(-16.1, 59.17) * mm});
            skArc(sketch, "E24.2.7", {"start": v(-15.8, 61.5) * mm, "mid": v(-15.9, 60.33) * mm, "end": v(-16.1, 59.17) * mm});
            skLineSegment(sketch, "E24.2.8", {"start": v(-15.8, 61.5) * mm, "end": v(-16.32, 63.12) * mm});
            skArc(sketch, "E24.2.9", {"start": v(-15.76, 64.13) * mm, "mid": v(-16.26, 63.75) * mm, "end": v(-16.32, 63.12) * mm});
            skArc(sketch, "E24.3.0", {"start": v(-27.66, 59.04) * mm, "mid": v(-28.1, 59.48) * mm, "end": v(-28.74, 59.46) * mm});
            skLineSegment(sketch, "E24.3.1", {"start": v(-27.04, 57.46) * mm, "end": v(-27.66, 59.04) * mm});
            skArc(sketch, "E24.3.2", {"start": v(-27.04, 57.46) * mm, "mid": v(-26.2, 56.62) * mm, "end": v(-25.32, 55.85) * mm});
            skArc(sketch, "E24.3.3", {"start": v(-25.32, 55.85) * mm, "mid": v(-24.94, 55.68) * mm, "end": v(-24.53, 55.73) * mm});
            skLineSegment(sketch, "E24.3.4", {"start": v(-24.53, 55.73) * mm, "end": v(-24.18, 55.87) * mm});
            skLineSegment(sketch, "E24.3.5", {"start": v(-23.83, 56.03) * mm, "end": v(-24.18, 55.87) * mm});
            skArc(sketch, "E24.3.6", {"start": v(-23.83, 56.03) * mm, "mid": v(-23.52, 56.3) * mm, "end": v(-23.38, 56.69) * mm});
            skArc(sketch, "E24.3.7", {"start": v(-23.38, 59.04) * mm, "mid": v(-23.33, 57.86) * mm, "end": v(-23.38, 56.69) * mm});
            skLineSegment(sketch, "E24.3.8", {"start": v(-23.38, 59.04) * mm, "end": v(-24.1, 60.58) * mm});
            skArc(sketch, "E24.3.9", {"start": v(-23.67, 61.65) * mm, "mid": v(-24.12, 61.21) * mm, "end": v(-24.1, 60.58) * mm});
            skArc(sketch, "E24.4.0", {"start": v(-34.85, 55.1) * mm, "mid": v(-35.34, 55.5) * mm, "end": v(-35.96, 55.39) * mm});
            skLineSegment(sketch, "E24.4.1", {"start": v(-34.03, 53.61) * mm, "end": v(-34.85, 55.1) * mm});
            skArc(sketch, "E24.4.2", {"start": v(-34.03, 53.61) * mm, "mid": v(-33.1, 52.89) * mm, "end": v(-32.12, 52.23) * mm});
            skArc(sketch, "E24.4.3", {"start": v(-32.12, 52.23) * mm, "mid": v(-31.72, 52.12) * mm, "end": v(-31.33, 52.21) * mm});
            skLineSegment(sketch, "E24.4.4", {"start": v(-31.33, 52.21) * mm, "end": v(-30.99, 52.4) * mm});
            skLineSegment(sketch, "E24.4.5", {"start": v(-30.66, 52.6) * mm, "end": v(-30.99, 52.4) * mm});
            skArc(sketch, "E24.4.6", {"start": v(-30.66, 52.6) * mm, "mid": v(-30.39, 52.9) * mm, "end": v(-30.3, 53.3) * mm});
            skArc(sketch, "E24.4.7", {"start": v(-30.6, 55.65) * mm, "mid": v(-30.4, 54.48) * mm, "end": v(-30.3, 53.3) * mm});
            skLineSegment(sketch, "E24.4.8", {"start": v(-30.6, 55.65) * mm, "end": v(-31.5, 57.08) * mm});
            skArc(sketch, "E24.4.9", {"start": v(-31.21, 58.2) * mm, "mid": v(-31.6, 57.7) * mm, "end": v(-31.5, 57.08) * mm});
            skArc(sketch, "E24.5.0", {"start": v(-41.48, 50.3) * mm, "mid": v(-42.02, 50.62) * mm, "end": v(-42.62, 50.44) * mm});
            skLineSegment(sketch, "E24.5.1", {"start": v(-40.48, 48.93) * mm, "end": v(-41.48, 50.3) * mm});
            skArc(sketch, "E24.5.2", {"start": v(-40.48, 48.93) * mm, "mid": v(-39.46, 48.32) * mm, "end": v(-38.41, 47.8) * mm});
            skArc(sketch, "E24.5.3", {"start": v(-38.41, 47.8) * mm, "mid": v(-38, 47.73) * mm, "end": v(-37.62, 47.88) * mm});
            skLineSegment(sketch, "E24.5.4", {"start": v(-37.62, 47.88) * mm, "end": v(-37.31, 48.1) * mm});
            skLineSegment(sketch, "E24.5.5", {"start": v(-37.02, 48.35) * mm, "end": v(-37.31, 48.1) * mm});
            skArc(sketch, "E24.5.6", {"start": v(-37.02, 48.35) * mm, "mid": v(-36.78, 48.68) * mm, "end": v(-36.74, 49.1) * mm});
            skArc(sketch, "E24.5.7", {"start": v(-37.32, 51.37) * mm, "mid": v(-37, 50.24) * mm, "end": v(-36.74, 49.1) * mm});
            skLineSegment(sketch, "E24.5.8", {"start": v(-37.32, 51.37) * mm, "end": v(-38.4, 52.68) * mm});
            skArc(sketch, "E24.5.9", {"start": v(-38.26, 53.83) * mm, "mid": v(-38.58, 53.29) * mm, "end": v(-38.4, 52.68) * mm});
            skArc(sketch, "E24.6.0", {"start": v(-47.46, 44.71) * mm, "mid": v(-48.03, 44.96) * mm, "end": v(-48.6, 44.7) * mm});
            skLineSegment(sketch, "E24.6.1", {"start": v(-46.29, 43.47) * mm, "end": v(-47.46, 44.71) * mm});
            skArc(sketch, "E24.6.2", {"start": v(-46.29, 43.47) * mm, "mid": v(-45.21, 43) * mm, "end": v(-44.1, 42.6) * mm});
            skArc(sketch, "E24.6.3", {"start": v(-44.1, 42.6) * mm, "mid": v(-43.69, 42.59) * mm, "end": v(-43.33, 42.78) * mm});
            skLineSegment(sketch, "E24.6.4", {"start": v(-43.33, 42.78) * mm, "end": v(-43.05, 43.05) * mm});
            skLineSegment(sketch, "E24.6.5", {"start": v(-42.78, 43.33) * mm, "end": v(-43.05, 43.05) * mm});
            skArc(sketch, "E24.6.6", {"start": v(-42.78, 43.33) * mm, "mid": v(-42.59, 43.69) * mm, "end": v(-42.6, 44.1) * mm});
            skArc(sketch, "E24.6.7", {"start": v(-43.47, 46.29) * mm, "mid": v(-43, 45.21) * mm, "end": v(-42.6, 44.1) * mm});
            skLineSegment(sketch, "E24.6.8", {"start": v(-43.47, 46.29) * mm, "end": v(-44.71, 47.46) * mm});
            skArc(sketch, "E24.6.9", {"start": v(-44.7, 48.6) * mm, "mid": v(-44.96, 48.03) * mm, "end": v(-44.71, 47.46) * mm});
            skArc(sketch, "E24.7.0", {"start": v(-52.68, 38.4) * mm, "mid": v(-53.29, 38.58) * mm, "end": v(-53.83, 38.26) * mm});
            skLineSegment(sketch, "E24.7.1", {"start": v(-51.37, 37.32) * mm, "end": v(-52.68, 38.4) * mm});
            skArc(sketch, "E24.7.2", {"start": v(-51.37, 37.32) * mm, "mid": v(-50.24, 37) * mm, "end": v(-49.1, 36.74) * mm});
            skArc(sketch, "E24.7.3", {"start": v(-49.1, 36.74) * mm, "mid": v(-48.68, 36.78) * mm, "end": v(-48.35, 37.02) * mm});
            skLineSegment(sketch, "E24.7.4", {"start": v(-48.35, 37.02) * mm, "end": v(-48.1, 37.31) * mm});
            skLineSegment(sketch, "E24.7.5", {"start": v(-47.88, 37.62) * mm, "end": v(-48.1, 37.31) * mm});
            skArc(sketch, "E24.7.6", {"start": v(-47.88, 37.62) * mm, "mid": v(-47.73, 38) * mm, "end": v(-47.8, 38.41) * mm});
            skArc(sketch, "E24.7.7", {"start": v(-48.93, 40.48) * mm, "mid": v(-48.32, 39.46) * mm, "end": v(-47.8, 38.41) * mm});
            skLineSegment(sketch, "E24.7.8", {"start": v(-48.93, 40.48) * mm, "end": v(-50.3, 41.48) * mm});
            skArc(sketch, "E24.7.9", {"start": v(-50.44, 42.62) * mm, "mid": v(-50.62, 42.02) * mm, "end": v(-50.3, 41.48) * mm});
            skArc(sketch, "E24.8.0", {"start": v(-57.08, 31.5) * mm, "mid": v(-57.7, 31.6) * mm, "end": v(-58.2, 31.21) * mm});
            skLineSegment(sketch, "E24.8.1", {"start": v(-55.65, 30.6) * mm, "end": v(-57.08, 31.5) * mm});
            skArc(sketch, "E24.8.2", {"start": v(-55.65, 30.6) * mm, "mid": v(-54.48, 30.4) * mm, "end": v(-53.3, 30.3) * mm});
            skArc(sketch, "E24.8.3", {"start": v(-53.3, 30.3) * mm, "mid": v(-52.9, 30.39) * mm, "end": v(-52.6, 30.66) * mm});
            skLineSegment(sketch, "E24.8.4", {"start": v(-52.6, 30.66) * mm, "end": v(-52.4, 30.99) * mm});
            skLineSegment(sketch, "E24.8.5", {"start": v(-52.21, 31.33) * mm, "end": v(-52.4, 30.99) * mm});
            skArc(sketch, "E24.8.6", {"start": v(-52.21, 31.33) * mm, "mid": v(-52.12, 31.72) * mm, "end": v(-52.23, 32.12) * mm});
            skArc(sketch, "E24.8.7", {"start": v(-53.61, 34.03) * mm, "mid": v(-52.89, 33.1) * mm, "end": v(-52.23, 32.12) * mm});
            skLineSegment(sketch, "E24.8.8", {"start": v(-53.61, 34.03) * mm, "end": v(-55.1, 34.85) * mm});
            skArc(sketch, "E24.8.9", {"start": v(-55.39, 35.96) * mm, "mid": v(-55.5, 35.34) * mm, "end": v(-55.1, 34.85) * mm});
            skArc(sketch, "E24.9.0", {"start": v(-60.58, 24.1) * mm, "mid": v(-61.21, 24.12) * mm, "end": v(-61.65, 23.67) * mm});
            skLineSegment(sketch, "E24.9.1", {"start": v(-59.04, 23.38) * mm, "end": v(-60.58, 24.1) * mm});
            skArc(sketch, "E24.9.2", {"start": v(-59.04, 23.38) * mm, "mid": v(-57.86, 23.33) * mm, "end": v(-56.69, 23.38) * mm});
            skArc(sketch, "E24.9.3", {"start": v(-56.69, 23.38) * mm, "mid": v(-56.3, 23.52) * mm, "end": v(-56.03, 23.83) * mm});
            skLineSegment(sketch, "E24.9.4", {"start": v(-56.03, 23.83) * mm, "end": v(-55.87, 24.18) * mm});
            skLineSegment(sketch, "E24.9.5", {"start": v(-55.73, 24.53) * mm, "end": v(-55.87, 24.18) * mm});
            skArc(sketch, "E24.9.6", {"start": v(-55.73, 24.53) * mm, "mid": v(-55.68, 24.94) * mm, "end": v(-55.85, 25.32) * mm});
            skArc(sketch, "E24.9.7", {"start": v(-57.46, 27.04) * mm, "mid": v(-56.62, 26.2) * mm, "end": v(-55.85, 25.32) * mm});
            skLineSegment(sketch, "E24.9.8", {"start": v(-57.46, 27.04) * mm, "end": v(-59.04, 27.66) * mm});
            skArc(sketch, "E24.9.9", {"start": v(-59.46, 28.74) * mm, "mid": v(-59.48, 28.1) * mm, "end": v(-59.04, 27.66) * mm});
            skArc(sketch, "E24.10.0", {"start": v(-63.12, 16.32) * mm, "mid": v(-63.75, 16.26) * mm, "end": v(-64.13, 15.76) * mm});
            skLineSegment(sketch, "E24.10.1", {"start": v(-61.5, 15.8) * mm, "end": v(-63.12, 16.32) * mm});
            skArc(sketch, "E24.10.2", {"start": v(-61.5, 15.8) * mm, "mid": v(-60.33, 15.9) * mm, "end": v(-59.17, 16.1) * mm});
            skArc(sketch, "E24.10.3", {"start": v(-59.17, 16.1) * mm, "mid": v(-58.8, 16.27) * mm, "end": v(-58.58, 16.62) * mm});
            skLineSegment(sketch, "E24.10.4", {"start": v(-58.58, 16.62) * mm, "end": v(-58.46, 16.98) * mm});
            skLineSegment(sketch, "E24.10.5", {"start": v(-58.36, 17.36) * mm, "end": v(-58.46, 16.98) * mm});
            skArc(sketch, "E24.10.6", {"start": v(-58.36, 17.36) * mm, "mid": v(-58.37, 17.77) * mm, "end": v(-58.58, 18.12) * mm});
            skArc(sketch, "E24.10.7", {"start": v(-60.4, 19.62) * mm, "mid": v(-59.46, 18.9) * mm, "end": v(-58.58, 18.12) * mm});
            skLineSegment(sketch, "E24.10.8", {"start": v(-60.4, 19.62) * mm, "end": v(-62.04, 20.05) * mm});
            skArc(sketch, "E24.10.9", {"start": v(-62.6, 21.06) * mm, "mid": v(-62.54, 20.43) * mm, "end": v(-62.04, 20.05) * mm});
            skArc(sketch, "E24.11.0", {"start": v(-64.67, 8.28) * mm, "mid": v(-65.29, 8.14) * mm, "end": v(-65.6, 7.6) * mm});
            skLineSegment(sketch, "E24.11.1", {"start": v(-63, 7.96) * mm, "end": v(-64.67, 8.28) * mm});
            skArc(sketch, "E24.11.2", {"start": v(-63, 7.96) * mm, "mid": v(-61.85, 8.21) * mm, "end": v(-60.72, 8.55) * mm});
            skArc(sketch, "E24.11.3", {"start": v(-60.72, 8.55) * mm, "mid": v(-60.38, 8.78) * mm, "end": v(-60.2, 9.15) * mm});
            skLineSegment(sketch, "E24.11.4", {"start": v(-60.2, 9.15) * mm, "end": v(-60.13, 9.52) * mm});
            skLineSegment(sketch, "E24.11.5", {"start": v(-60.08, 9.9) * mm, "end": v(-60.13, 9.52) * mm});
            skArc(sketch, "E24.11.6", {"start": v(-60.08, 9.9) * mm, "mid": v(-60.14, 10.31) * mm, "end": v(-60.39, 10.63) * mm});
            skArc(sketch, "E24.11.7", {"start": v(-62.38, 11.9) * mm, "mid": v(-61.36, 11.3) * mm, "end": v(-60.39, 10.63) * mm});
            skLineSegment(sketch, "E24.11.8", {"start": v(-62.38, 11.9) * mm, "end": v(-64.06, 12.11) * mm});
            skArc(sketch, "E24.11.9", {"start": v(-64.74, 13.05) * mm, "mid": v(-64.6, 12.43) * mm, "end": v(-64.06, 12.11) * mm});
            skArc(sketch, "E24.12.0", {"start": v(-65.2, 0.1) * mm, "mid": v(-65.8, -0.1) * mm, "end": v(-66.04, -0.69) * mm});
            skLineSegment(sketch, "E24.12.1", {"start": v(-63.5, 0) * mm, "end": v(-65.2, 0.1) * mm});
            skArc(sketch, "E24.12.2", {"start": v(-63.5, 0) * mm, "mid": v(-62.39, 0.4) * mm, "end": v(-61.31, 0.87) * mm});
            skArc(sketch, "E24.12.3", {"start": v(-61.31, 0.87) * mm, "mid": v(-61, 1.14) * mm, "end": v(-60.87, 1.53) * mm});
            skLineSegment(sketch, "E24.12.4", {"start": v(-60.87, 1.53) * mm, "end": v(-60.85, 1.91) * mm});
            skLineSegment(sketch, "E24.12.5", {"start": v(-60.85, 2.3) * mm, "end": v(-60.85, 1.91) * mm});
            skArc(sketch, "E24.12.6", {"start": v(-60.85, 2.3) * mm, "mid": v(-60.95, 2.7) * mm, "end": v(-61.25, 2.98) * mm});
            skArc(sketch, "E24.12.7", {"start": v(-63.37, 3.99) * mm, "mid": v(-62.3, 3.52) * mm, "end": v(-61.25, 2.98) * mm});
            skLineSegment(sketch, "E24.12.8", {"start": v(-63.37, 3.99) * mm, "end": v(-65.08, 3.99) * mm});
            skArc(sketch, "E24.12.9", {"start": v(-65.86, 4.83) * mm, "mid": v(-65.65, 4.24) * mm, "end": v(-65.08, 3.99) * mm});
            skArc(sketch, "E24.13.0", {"start": v(-64.7, -8.07) * mm, "mid": v(-65.26, -8.35) * mm, "end": v(-65.43, -8.96) * mm});
            skLineSegment(sketch, "E24.13.1", {"start": v(-63, -7.96) * mm, "end": v(-64.7, -8.07) * mm});
            skArc(sketch, "E24.13.2", {"start": v(-63, -7.96) * mm, "mid": v(-61.95, -7.43) * mm, "end": v(-60.94, -6.82) * mm});
            skArc(sketch, "E24.13.3", {"start": v(-60.94, -6.82) * mm, "mid": v(-60.66, -6.51) * mm, "end": v(-60.58, -6.11) * mm});
            skLineSegment(sketch, "E24.13.4", {"start": v(-60.58, -6.11) * mm, "end": v(-60.6, -5.73) * mm});
            skLineSegment(sketch, "E24.13.5", {"start": v(-60.65, -5.35) * mm, "end": v(-60.6, -5.73) * mm});
            skArc(sketch, "E24.13.6", {"start": v(-60.65, -5.35) * mm, "mid": v(-60.81, -4.97) * mm, "end": v(-61.14, -4.72) * mm});
            skArc(sketch, "E24.13.7", {"start": v(-63.37, -3.99) * mm, "mid": v(-62.24, -4.31) * mm, "end": v(-61.14, -4.72) * mm});
            skLineSegment(sketch, "E24.13.8", {"start": v(-63.37, -3.99) * mm, "end": v(-65.06, -4.2) * mm});
            skArc(sketch, "E24.13.9", {"start": v(-65.95, -3.46) * mm, "mid": v(-65.67, -4.02) * mm, "end": v(-65.06, -4.2) * mm});
            skArc(sketch, "E24.14.0", {"start": v(-63.18, -16.11) * mm, "mid": v(-63.7, -16.47) * mm, "end": v(-63.8, -17.09) * mm});
            skLineSegment(sketch, "E24.14.1", {"start": v(-61.5, -15.8) * mm, "end": v(-63.18, -16.11) * mm});
            skArc(sketch, "E24.14.2", {"start": v(-61.5, -15.8) * mm, "mid": v(-60.53, -15.13) * mm, "end": v(-59.6, -14.4) * mm});
            skArc(sketch, "E24.14.3", {"start": v(-59.6, -14.4) * mm, "mid": v(-59.37, -14.07) * mm, "end": v(-59.34, -13.66) * mm});
            skLineSegment(sketch, "E24.14.4", {"start": v(-59.34, -13.66) * mm, "end": v(-59.41, -13.28) * mm});
            skLineSegment(sketch, "E24.14.5", {"start": v(-59.5, -12.9) * mm, "end": v(-59.41, -13.28) * mm});
            skArc(sketch, "E24.14.6", {"start": v(-59.5, -12.9) * mm, "mid": v(-59.7, -12.55) * mm, "end": v(-60.06, -12.34) * mm});
            skArc(sketch, "E24.14.7", {"start": v(-62.38, -11.9) * mm, "mid": v(-61.21, -12.08) * mm, "end": v(-60.06, -12.34) * mm});
            skLineSegment(sketch, "E24.14.8", {"start": v(-62.38, -11.9) * mm, "end": v(-64.02, -12.32) * mm});
            skArc(sketch, "E24.14.9", {"start": v(-65, -11.7) * mm, "mid": v(-64.65, -12.22) * mm, "end": v(-64.02, -12.32) * mm});
            skArc(sketch, "E24.15.0", {"start": v(-60.66, -23.9) * mm, "mid": v(-61.13, -24.32) * mm, "end": v(-61.15, -24.95) * mm});
            skLineSegment(sketch, "E24.15.1", {"start": v(-59.04, -23.38) * mm, "end": v(-60.66, -23.9) * mm});
            skArc(sketch, "E24.15.2", {"start": v(-59.04, -23.38) * mm, "mid": v(-58.15, -22.6) * mm, "end": v(-57.33, -21.76) * mm});
            skArc(sketch, "E24.15.3", {"start": v(-57.33, -21.76) * mm, "mid": v(-57.14, -21.4) * mm, "end": v(-57.16, -20.99) * mm});
            skLineSegment(sketch, "E24.15.4", {"start": v(-57.16, -20.99) * mm, "end": v(-57.28, -20.62) * mm});
            skLineSegment(sketch, "E24.15.5", {"start": v(-57.42, -20.26) * mm, "end": v(-57.28, -20.62) * mm});
            skArc(sketch, "E24.15.6", {"start": v(-57.42, -20.26) * mm, "mid": v(-57.66, -19.93) * mm, "end": v(-58.04, -19.77) * mm});
            skArc(sketch, "E24.15.7", {"start": v(-60.4, -19.62) * mm, "mid": v(-59.21, -19.65) * mm, "end": v(-58.04, -19.77) * mm});
            skLineSegment(sketch, "E24.15.8", {"start": v(-60.4, -19.62) * mm, "end": v(-61.98, -20.25) * mm});
            skArc(sketch, "E24.15.9", {"start": v(-63.02, -19.75) * mm, "mid": v(-62.6, -20.23) * mm, "end": v(-61.98, -20.25) * mm});
            skArc(sketch, "E24.16.0", {"start": v(-57.19, -31.32) * mm, "mid": v(-57.6, -31.79) * mm, "end": v(-57.54, -32.42) * mm});
            skLineSegment(sketch, "E24.16.1", {"start": v(-55.65, -30.6) * mm, "end": v(-57.19, -31.32) * mm});
            skArc(sketch, "E24.16.2", {"start": v(-55.65, -30.6) * mm, "mid": v(-54.86, -29.71) * mm, "end": v(-54.15, -28.77) * mm});
            skArc(sketch, "E24.16.3", {"start": v(-54.15, -28.77) * mm, "mid": v(-54, -28.39) * mm, "end": v(-54.08, -27.98) * mm});
            skLineSegment(sketch, "E24.16.4", {"start": v(-54.08, -27.98) * mm, "end": v(-54.24, -27.64) * mm});
            skLineSegment(sketch, "E24.16.5", {"start": v(-54.43, -27.3) * mm, "end": v(-54.24, -27.64) * mm});
            skArc(sketch, "E24.16.6", {"start": v(-54.43, -27.3) * mm, "mid": v(-54.71, -27) * mm, "end": v(-55.1, -26.9) * mm});
            skArc(sketch, "E24.16.7", {"start": v(-57.46, -27.04) * mm, "mid": v(-56.28, -26.92) * mm, "end": v(-55.1, -26.9) * mm});
            skLineSegment(sketch, "E24.16.8", {"start": v(-57.46, -27.04) * mm, "end": v(-58.95, -27.86) * mm});
            skArc(sketch, "E24.16.9", {"start": v(-60.04, -27.5) * mm, "mid": v(-59.58, -27.91) * mm, "end": v(-58.95, -27.86) * mm});
            skArc(sketch, "E24.17.0", {"start": v(-52.81, -38.24) * mm, "mid": v(-53.16, -38.76) * mm, "end": v(-53.02, -39.37) * mm});
            skLineSegment(sketch, "E24.17.1", {"start": v(-51.37, -37.32) * mm, "end": v(-52.81, -38.24) * mm});
            skArc(sketch, "E24.17.2", {"start": v(-51.37, -37.32) * mm, "mid": v(-50.7, -36.35) * mm, "end": v(-50.11, -35.33) * mm});
            skArc(sketch, "E24.17.3", {"start": v(-50.11, -35.33) * mm, "mid": v(-50.02, -34.93) * mm, "end": v(-50.14, -34.54) * mm});
            skLineSegment(sketch, "E24.17.4", {"start": v(-50.14, -34.54) * mm, "end": v(-50.35, -34.22) * mm});
            skLineSegment(sketch, "E24.17.5", {"start": v(-50.58, -33.9) * mm, "end": v(-50.35, -34.22) * mm});
            skArc(sketch, "E24.17.6", {"start": v(-50.58, -33.9) * mm, "mid": v(-50.9, -33.65) * mm, "end": v(-51.3, -33.59) * mm});
            skArc(sketch, "E24.17.7", {"start": v(-53.61, -34.03) * mm, "mid": v(-52.47, -33.76) * mm, "end": v(-51.3, -33.59) * mm});
            skLineSegment(sketch, "E24.17.8", {"start": v(-53.61, -34.03) * mm, "end": v(-55, -35.03) * mm});
            skArc(sketch, "E24.17.9", {"start": v(-56.12, -34.8) * mm, "mid": v(-55.6, -35.16) * mm, "end": v(-55, -35.03) * mm});
            skArc(sketch, "E24.18.0", {"start": v(-47.6, -44.55) * mm, "mid": v(-47.89, -45.12) * mm, "end": v(-47.67, -45.7) * mm});
            skLineSegment(sketch, "E24.18.1", {"start": v(-46.29, -43.47) * mm, "end": v(-47.6, -44.55) * mm});
            skArc(sketch, "E24.18.2", {"start": v(-46.29, -43.47) * mm, "mid": v(-45.75, -42.42) * mm, "end": v(-45.3, -41.34) * mm});
            skArc(sketch, "E24.18.3", {"start": v(-45.3, -41.34) * mm, "mid": v(-45.25, -40.93) * mm, "end": v(-45.42, -40.55) * mm});
            skLineSegment(sketch, "E24.18.4", {"start": v(-45.42, -40.55) * mm, "end": v(-45.66, -40.26) * mm});
            skLineSegment(sketch, "E24.18.5", {"start": v(-45.93, -39.98) * mm, "end": v(-45.66, -40.26) * mm});
            skArc(sketch, "E24.18.6", {"start": v(-45.93, -39.98) * mm, "mid": v(-46.28, -39.76) * mm, "end": v(-46.69, -39.75) * mm});
            skArc(sketch, "E24.18.7", {"start": v(-48.93, -40.48) * mm, "mid": v(-47.82, -40.07) * mm, "end": v(-46.69, -39.75) * mm});
            skLineSegment(sketch, "E24.18.8", {"start": v(-48.93, -40.48) * mm, "end": v(-50.17, -41.64) * mm});
            skArc(sketch, "E24.18.9", {"start": v(-51.32, -41.56) * mm, "mid": v(-50.76, -41.85) * mm, "end": v(-50.17, -41.64) * mm});
            skArc(sketch, "E24.19.0", {"start": v(-41.64, -50.17) * mm, "mid": v(-41.85, -50.76) * mm, "end": v(-41.56, -51.32) * mm});
            skLineSegment(sketch, "E24.19.1", {"start": v(-40.48, -48.93) * mm, "end": v(-41.64, -50.17) * mm});
            skArc(sketch, "E24.19.2", {"start": v(-40.48, -48.93) * mm, "mid": v(-40.07, -47.82) * mm, "end": v(-39.75, -46.69) * mm});
            skArc(sketch, "E24.19.3", {"start": v(-39.75, -46.69) * mm, "mid": v(-39.76, -46.28) * mm, "end": v(-39.98, -45.93) * mm});
            skLineSegment(sketch, "E24.19.4", {"start": v(-39.98, -45.93) * mm, "end": v(-40.26, -45.66) * mm});
            skLineSegment(sketch, "E24.19.5", {"start": v(-40.55, -45.42) * mm, "end": v(-40.26, -45.66) * mm});
            skArc(sketch, "E24.19.6", {"start": v(-40.55, -45.42) * mm, "mid": v(-40.93, -45.25) * mm, "end": v(-41.34, -45.3) * mm});
            skArc(sketch, "E24.19.7", {"start": v(-43.47, -46.29) * mm, "mid": v(-42.42, -45.75) * mm, "end": v(-41.34, -45.3) * mm});
            skLineSegment(sketch, "E24.19.8", {"start": v(-43.47, -46.29) * mm, "end": v(-44.55, -47.6) * mm});
            skArc(sketch, "E24.19.9", {"start": v(-45.7, -47.67) * mm, "mid": v(-45.12, -47.89) * mm, "end": v(-44.55, -47.6) * mm});
            skArc(sketch, "E24.20.0", {"start": v(-35.03, -55) * mm, "mid": v(-35.16, -55.6) * mm, "end": v(-34.8, -56.12) * mm});
            skLineSegment(sketch, "E24.20.1", {"start": v(-34.03, -53.61) * mm, "end": v(-35.03, -55) * mm});
            skArc(sketch, "E24.20.2", {"start": v(-34.03, -53.61) * mm, "mid": v(-33.76, -52.47) * mm, "end": v(-33.59, -51.3) * mm});
            skArc(sketch, "E24.20.3", {"start": v(-33.59, -51.3) * mm, "mid": v(-33.65, -50.9) * mm, "end": v(-33.9, -50.58) * mm});
            skLineSegment(sketch, "E24.20.4", {"start": v(-33.9, -50.58) * mm, "end": v(-34.22, -50.35) * mm});
            skLineSegment(sketch, "E24.20.5", {"start": v(-34.54, -50.14) * mm, "end": v(-34.22, -50.35) * mm});
            skArc(sketch, "E24.20.6", {"start": v(-34.54, -50.14) * mm, "mid": v(-34.93, -50.02) * mm, "end": v(-35.33, -50.11) * mm});
            skArc(sketch, "E24.20.7", {"start": v(-37.32, -51.37) * mm, "mid": v(-36.35, -50.7) * mm, "end": v(-35.33, -50.11) * mm});
            skLineSegment(sketch, "E24.20.8", {"start": v(-37.32, -51.37) * mm, "end": v(-38.24, -52.81) * mm});
            skArc(sketch, "E24.20.9", {"start": v(-39.37, -53.02) * mm, "mid": v(-38.76, -53.16) * mm, "end": v(-38.24, -52.81) * mm});
            skArc(sketch, "E24.21.0", {"start": v(-27.86, -58.95) * mm, "mid": v(-27.91, -59.58) * mm, "end": v(-27.5, -60.04) * mm});
            skLineSegment(sketch, "E24.21.1", {"start": v(-27.04, -57.46) * mm, "end": v(-27.86, -58.95) * mm});
            skArc(sketch, "E24.21.2", {"start": v(-27.04, -57.46) * mm, "mid": v(-26.92, -56.28) * mm, "end": v(-26.9, -55.1) * mm});
            skArc(sketch, "E24.21.3", {"start": v(-26.9, -55.1) * mm, "mid": v(-27, -54.71) * mm, "end": v(-27.3, -54.43) * mm});
            skLineSegment(sketch, "E24.21.4", {"start": v(-27.3, -54.43) * mm, "end": v(-27.64, -54.24) * mm});
            skLineSegment(sketch, "E24.21.5", {"start": v(-27.98, -54.08) * mm, "end": v(-27.64, -54.24) * mm});
            skArc(sketch, "E24.21.6", {"start": v(-27.98, -54.08) * mm, "mid": v(-28.39, -54) * mm, "end": v(-28.77, -54.15) * mm});
            skArc(sketch, "E24.21.7", {"start": v(-30.6, -55.65) * mm, "mid": v(-29.71, -54.86) * mm, "end": v(-28.77, -54.15) * mm});
            skLineSegment(sketch, "E24.21.8", {"start": v(-30.6, -55.65) * mm, "end": v(-31.32, -57.19) * mm});
            skArc(sketch, "E24.21.9", {"start": v(-32.42, -57.54) * mm, "mid": v(-31.79, -57.6) * mm, "end": v(-31.32, -57.19) * mm});
            skArc(sketch, "E24.22.0", {"start": v(-20.25, -61.98) * mm, "mid": v(-20.23, -62.6) * mm, "end": v(-19.75, -63.02) * mm});
            skLineSegment(sketch, "E24.22.1", {"start": v(-19.62, -60.4) * mm, "end": v(-20.25, -61.98) * mm});
            skArc(sketch, "E24.22.2", {"start": v(-19.62, -60.4) * mm, "mid": v(-19.65, -59.21) * mm, "end": v(-19.77, -58.04) * mm});
            skArc(sketch, "E24.22.3", {"start": v(-19.77, -58.04) * mm, "mid": v(-19.93, -57.66) * mm, "end": v(-20.26, -57.42) * mm});
            skLineSegment(sketch, "E24.22.4", {"start": v(-20.26, -57.42) * mm, "end": v(-20.62, -57.28) * mm});
            skLineSegment(sketch, "E24.22.5", {"start": v(-20.99, -57.16) * mm, "end": v(-20.62, -57.28) * mm});
            skArc(sketch, "E24.22.6", {"start": v(-20.99, -57.16) * mm, "mid": v(-21.4, -57.14) * mm, "end": v(-21.76, -57.33) * mm});
            skArc(sketch, "E24.22.7", {"start": v(-23.38, -59.04) * mm, "mid": v(-22.6, -58.15) * mm, "end": v(-21.76, -57.33) * mm});
            skLineSegment(sketch, "E24.22.8", {"start": v(-23.38, -59.04) * mm, "end": v(-23.9, -60.66) * mm});
            skArc(sketch, "E24.22.9", {"start": v(-24.95, -61.15) * mm, "mid": v(-24.32, -61.13) * mm, "end": v(-23.9, -60.66) * mm});
            skArc(sketch, "E24.23.0", {"start": v(-12.32, -64.02) * mm, "mid": v(-12.22, -64.65) * mm, "end": v(-11.7, -65) * mm});
            skLineSegment(sketch, "E24.23.1", {"start": v(-11.9, -62.38) * mm, "end": v(-12.32, -64.02) * mm});
            skArc(sketch, "E24.23.2", {"start": v(-11.9, -62.38) * mm, "mid": v(-12.08, -61.21) * mm, "end": v(-12.34, -60.06) * mm});
            skArc(sketch, "E24.23.3", {"start": v(-12.34, -60.06) * mm, "mid": v(-12.55, -59.7) * mm, "end": v(-12.9, -59.5) * mm});
            skLineSegment(sketch, "E24.23.4", {"start": v(-12.9, -59.5) * mm, "end": v(-13.28, -59.41) * mm});
            skLineSegment(sketch, "E24.23.5", {"start": v(-13.66, -59.34) * mm, "end": v(-13.28, -59.41) * mm});
            skArc(sketch, "E24.23.6", {"start": v(-13.66, -59.34) * mm, "mid": v(-14.07, -59.37) * mm, "end": v(-14.4, -59.6) * mm});
            skArc(sketch, "E24.23.7", {"start": v(-15.8, -61.5) * mm, "mid": v(-15.13, -60.53) * mm, "end": v(-14.4, -59.6) * mm});
            skLineSegment(sketch, "E24.23.8", {"start": v(-15.8, -61.5) * mm, "end": v(-16.11, -63.18) * mm});
            skArc(sketch, "E24.23.9", {"start": v(-17.09, -63.8) * mm, "mid": v(-16.47, -63.7) * mm, "end": v(-16.11, -63.18) * mm});
            skArc(sketch, "E24.24.0", {"start": v(-4.2, -65.06) * mm, "mid": v(-4.02, -65.67) * mm, "end": v(-3.46, -65.95) * mm});
            skLineSegment(sketch, "E24.24.1", {"start": v(-3.99, -63.37) * mm, "end": v(-4.2, -65.06) * mm});
            skArc(sketch, "E24.24.2", {"start": v(-3.99, -63.37) * mm, "mid": v(-4.31, -62.24) * mm, "end": v(-4.72, -61.14) * mm});
            skArc(sketch, "E24.24.3", {"start": v(-4.72, -61.14) * mm, "mid": v(-4.97, -60.81) * mm, "end": v(-5.35, -60.65) * mm});
            skLineSegment(sketch, "E24.24.4", {"start": v(-5.35, -60.65) * mm, "end": v(-5.73, -60.6) * mm});
            skLineSegment(sketch, "E24.24.5", {"start": v(-6.11, -60.58) * mm, "end": v(-5.73, -60.6) * mm});
            skArc(sketch, "E24.24.6", {"start": v(-6.11, -60.58) * mm, "mid": v(-6.51, -60.66) * mm, "end": v(-6.82, -60.94) * mm});
            skArc(sketch, "E24.24.7", {"start": v(-7.96, -63) * mm, "mid": v(-7.43, -61.95) * mm, "end": v(-6.82, -60.94) * mm});
            skLineSegment(sketch, "E24.24.8", {"start": v(-7.96, -63) * mm, "end": v(-8.07, -64.7) * mm});
            skArc(sketch, "E24.24.9", {"start": v(-8.96, -65.43) * mm, "mid": v(-8.35, -65.26) * mm, "end": v(-8.07, -64.7) * mm});
            skArc(sketch, "E24.25.0", {"start": v(3.99, -65.08) * mm, "mid": v(4.24, -65.65) * mm, "end": v(4.83, -65.86) * mm});
            skLineSegment(sketch, "E24.25.1", {"start": v(3.99, -63.37) * mm, "end": v(3.99, -65.08) * mm});
            skArc(sketch, "E24.25.2", {"start": v(3.99, -63.37) * mm, "mid": v(3.52, -62.3) * mm, "end": v(2.98, -61.25) * mm});
            skArc(sketch, "E24.25.3", {"start": v(2.98, -61.25) * mm, "mid": v(2.7, -60.95) * mm, "end": v(2.3, -60.85) * mm});
            skLineSegment(sketch, "E24.25.4", {"start": v(2.3, -60.85) * mm, "end": v(1.91, -60.85) * mm});
            skLineSegment(sketch, "E24.25.5", {"start": v(1.53, -60.87) * mm, "end": v(1.91, -60.85) * mm});
            skArc(sketch, "E24.25.6", {"start": v(1.53, -60.87) * mm, "mid": v(1.14, -61) * mm, "end": v(0.87, -61.31) * mm});
            skArc(sketch, "E24.25.7", {"start": v(0, -63.5) * mm, "mid": v(0.4, -62.39) * mm, "end": v(0.87, -61.31) * mm});
            skLineSegment(sketch, "E24.25.8", {"start": v(0, -63.5) * mm, "end": v(0.1, -65.2) * mm});
            skArc(sketch, "E24.25.9", {"start": v(-0.69, -66.04) * mm, "mid": v(-0.1, -65.8) * mm, "end": v(0.1, -65.2) * mm});
            skArc(sketch, "E24.26.0", {"start": v(12.11, -64.06) * mm, "mid": v(12.43, -64.6) * mm, "end": v(13.05, -64.74) * mm});
            skLineSegment(sketch, "E24.26.1", {"start": v(11.9, -62.38) * mm, "end": v(12.11, -64.06) * mm});
            skArc(sketch, "E24.26.2", {"start": v(11.9, -62.38) * mm, "mid": v(11.3, -61.36) * mm, "end": v(10.63, -60.39) * mm});
            skArc(sketch, "E24.26.3", {"start": v(10.63, -60.39) * mm, "mid": v(10.31, -60.14) * mm, "end": v(9.9, -60.08) * mm});
            skLineSegment(sketch, "E24.26.4", {"start": v(9.9, -60.08) * mm, "end": v(9.52, -60.13) * mm});
            skLineSegment(sketch, "E24.26.5", {"start": v(9.15, -60.2) * mm, "end": v(9.52, -60.13) * mm});
            skArc(sketch, "E24.26.6", {"start": v(9.15, -60.2) * mm, "mid": v(8.78, -60.38) * mm, "end": v(8.55, -60.72) * mm});
            skArc(sketch, "E24.26.7", {"start": v(7.96, -63) * mm, "mid": v(8.21, -61.85) * mm, "end": v(8.55, -60.72) * mm});
            skLineSegment(sketch, "E24.26.8", {"start": v(7.96, -63) * mm, "end": v(8.28, -64.67) * mm});
            skArc(sketch, "E24.26.9", {"start": v(7.6, -65.6) * mm, "mid": v(8.14, -65.29) * mm, "end": v(8.28, -64.67) * mm});
            skArc(sketch, "E24.27.0", {"start": v(20.05, -62.04) * mm, "mid": v(20.43, -62.54) * mm, "end": v(21.06, -62.6) * mm});
            skLineSegment(sketch, "E24.27.1", {"start": v(19.62, -60.4) * mm, "end": v(20.05, -62.04) * mm});
            skArc(sketch, "E24.27.2", {"start": v(19.62, -60.4) * mm, "mid": v(18.9, -59.46) * mm, "end": v(18.12, -58.58) * mm});
            skArc(sketch, "E24.27.3", {"start": v(18.12, -58.58) * mm, "mid": v(17.77, -58.37) * mm, "end": v(17.36, -58.36) * mm});
            skLineSegment(sketch, "E24.27.4", {"start": v(17.36, -58.36) * mm, "end": v(16.98, -58.46) * mm});
            skLineSegment(sketch, "E24.27.5", {"start": v(16.62, -58.58) * mm, "end": v(16.98, -58.46) * mm});
            skArc(sketch, "E24.27.6", {"start": v(16.62, -58.58) * mm, "mid": v(16.27, -58.8) * mm, "end": v(16.1, -59.17) * mm});
            skArc(sketch, "E24.27.7", {"start": v(15.8, -61.5) * mm, "mid": v(15.9, -60.33) * mm, "end": v(16.1, -59.17) * mm});
            skLineSegment(sketch, "E24.27.8", {"start": v(15.8, -61.5) * mm, "end": v(16.32, -63.12) * mm});
            skArc(sketch, "E24.27.9", {"start": v(15.76, -64.13) * mm, "mid": v(16.26, -63.75) * mm, "end": v(16.32, -63.12) * mm});
            skArc(sketch, "E24.28.0", {"start": v(27.66, -59.04) * mm, "mid": v(28.1, -59.48) * mm, "end": v(28.74, -59.46) * mm});
            skLineSegment(sketch, "E24.28.1", {"start": v(27.04, -57.46) * mm, "end": v(27.66, -59.04) * mm});
            skArc(sketch, "E24.28.2", {"start": v(27.04, -57.46) * mm, "mid": v(26.2, -56.62) * mm, "end": v(25.32, -55.85) * mm});
            skArc(sketch, "E24.28.3", {"start": v(25.32, -55.85) * mm, "mid": v(24.94, -55.68) * mm, "end": v(24.53, -55.73) * mm});
            skLineSegment(sketch, "E24.28.4", {"start": v(24.53, -55.73) * mm, "end": v(24.18, -55.87) * mm});
            skLineSegment(sketch, "E24.28.5", {"start": v(23.83, -56.03) * mm, "end": v(24.18, -55.87) * mm});
            skArc(sketch, "E24.28.6", {"start": v(23.83, -56.03) * mm, "mid": v(23.52, -56.3) * mm, "end": v(23.38, -56.69) * mm});
            skArc(sketch, "E24.28.7", {"start": v(23.38, -59.04) * mm, "mid": v(23.33, -57.86) * mm, "end": v(23.38, -56.69) * mm});
            skLineSegment(sketch, "E24.28.8", {"start": v(23.38, -59.04) * mm, "end": v(24.1, -60.58) * mm});
            skArc(sketch, "E24.28.9", {"start": v(23.67, -61.65) * mm, "mid": v(24.12, -61.21) * mm, "end": v(24.1, -60.58) * mm});
            skArc(sketch, "E24.29.0", {"start": v(34.85, -55.1) * mm, "mid": v(35.34, -55.5) * mm, "end": v(35.96, -55.39) * mm});
            skLineSegment(sketch, "E24.29.1", {"start": v(34.03, -53.61) * mm, "end": v(34.85, -55.1) * mm});
            skArc(sketch, "E24.29.2", {"start": v(34.03, -53.61) * mm, "mid": v(33.1, -52.89) * mm, "end": v(32.12, -52.23) * mm});
            skArc(sketch, "E24.29.3", {"start": v(32.12, -52.23) * mm, "mid": v(31.72, -52.12) * mm, "end": v(31.33, -52.21) * mm});
            skLineSegment(sketch, "E24.29.4", {"start": v(31.33, -52.21) * mm, "end": v(30.99, -52.4) * mm});
            skLineSegment(sketch, "E24.29.5", {"start": v(30.66, -52.6) * mm, "end": v(30.99, -52.4) * mm});
            skArc(sketch, "E24.29.6", {"start": v(30.66, -52.6) * mm, "mid": v(30.39, -52.9) * mm, "end": v(30.3, -53.3) * mm});
            skArc(sketch, "E24.29.7", {"start": v(30.6, -55.65) * mm, "mid": v(30.4, -54.48) * mm, "end": v(30.3, -53.3) * mm});
            skLineSegment(sketch, "E24.29.8", {"start": v(30.6, -55.65) * mm, "end": v(31.5, -57.08) * mm});
            skArc(sketch, "E24.29.9", {"start": v(31.21, -58.2) * mm, "mid": v(31.6, -57.7) * mm, "end": v(31.5, -57.08) * mm});
            skArc(sketch, "E24.30.0", {"start": v(41.48, -50.3) * mm, "mid": v(42.02, -50.62) * mm, "end": v(42.62, -50.44) * mm});
            skLineSegment(sketch, "E24.30.1", {"start": v(40.48, -48.93) * mm, "end": v(41.48, -50.3) * mm});
            skArc(sketch, "E24.30.2", {"start": v(40.48, -48.93) * mm, "mid": v(39.46, -48.32) * mm, "end": v(38.41, -47.8) * mm});
            skArc(sketch, "E24.30.3", {"start": v(38.41, -47.8) * mm, "mid": v(38, -47.73) * mm, "end": v(37.62, -47.88) * mm});
            skLineSegment(sketch, "E24.30.4", {"start": v(37.62, -47.88) * mm, "end": v(37.31, -48.1) * mm});
            skLineSegment(sketch, "E24.30.5", {"start": v(37.02, -48.35) * mm, "end": v(37.31, -48.1) * mm});
            skArc(sketch, "E24.30.6", {"start": v(37.02, -48.35) * mm, "mid": v(36.78, -48.68) * mm, "end": v(36.74, -49.1) * mm});
            skArc(sketch, "E24.30.7", {"start": v(37.32, -51.37) * mm, "mid": v(37, -50.24) * mm, "end": v(36.74, -49.1) * mm});
            skLineSegment(sketch, "E24.30.8", {"start": v(37.32, -51.37) * mm, "end": v(38.4, -52.68) * mm});
            skArc(sketch, "E24.30.9", {"start": v(38.26, -53.83) * mm, "mid": v(38.58, -53.29) * mm, "end": v(38.4, -52.68) * mm});
            skArc(sketch, "E24.31.0", {"start": v(47.46, -44.71) * mm, "mid": v(48.03, -44.96) * mm, "end": v(48.6, -44.7) * mm});
            skLineSegment(sketch, "E24.31.1", {"start": v(46.29, -43.47) * mm, "end": v(47.46, -44.71) * mm});
            skArc(sketch, "E24.31.2", {"start": v(46.29, -43.47) * mm, "mid": v(45.21, -43) * mm, "end": v(44.1, -42.6) * mm});
            skArc(sketch, "E24.31.3", {"start": v(44.1, -42.6) * mm, "mid": v(43.69, -42.59) * mm, "end": v(43.33, -42.78) * mm});
            skLineSegment(sketch, "E24.31.4", {"start": v(43.33, -42.78) * mm, "end": v(43.05, -43.05) * mm});
            skLineSegment(sketch, "E24.31.5", {"start": v(42.78, -43.33) * mm, "end": v(43.05, -43.05) * mm});
            skArc(sketch, "E24.31.6", {"start": v(42.78, -43.33) * mm, "mid": v(42.59, -43.69) * mm, "end": v(42.6, -44.1) * mm});
            skArc(sketch, "E24.31.7", {"start": v(43.47, -46.29) * mm, "mid": v(43, -45.21) * mm, "end": v(42.6, -44.1) * mm});
            skLineSegment(sketch, "E24.31.8", {"start": v(43.47, -46.29) * mm, "end": v(44.71, -47.46) * mm});
            skArc(sketch, "E24.31.9", {"start": v(44.7, -48.6) * mm, "mid": v(44.96, -48.03) * mm, "end": v(44.71, -47.46) * mm});
            skArc(sketch, "E24.32.0", {"start": v(52.68, -38.4) * mm, "mid": v(53.29, -38.58) * mm, "end": v(53.83, -38.26) * mm});
            skLineSegment(sketch, "E24.32.1", {"start": v(51.37, -37.32) * mm, "end": v(52.68, -38.4) * mm});
            skArc(sketch, "E24.32.2", {"start": v(51.37, -37.32) * mm, "mid": v(50.24, -37) * mm, "end": v(49.1, -36.74) * mm});
            skArc(sketch, "E24.32.3", {"start": v(49.1, -36.74) * mm, "mid": v(48.68, -36.78) * mm, "end": v(48.35, -37.02) * mm});
            skLineSegment(sketch, "E24.32.4", {"start": v(48.35, -37.02) * mm, "end": v(48.1, -37.31) * mm});
            skLineSegment(sketch, "E24.32.5", {"start": v(47.88, -37.62) * mm, "end": v(48.1, -37.31) * mm});
            skArc(sketch, "E24.32.6", {"start": v(47.88, -37.62) * mm, "mid": v(47.73, -38) * mm, "end": v(47.8, -38.41) * mm});
            skArc(sketch, "E24.32.7", {"start": v(48.93, -40.48) * mm, "mid": v(48.32, -39.46) * mm, "end": v(47.8, -38.41) * mm});
            skLineSegment(sketch, "E24.32.8", {"start": v(48.93, -40.48) * mm, "end": v(50.3, -41.48) * mm});
            skArc(sketch, "E24.32.9", {"start": v(50.44, -42.62) * mm, "mid": v(50.62, -42.02) * mm, "end": v(50.3, -41.48) * mm});
            skArc(sketch, "E24.33.0", {"start": v(57.08, -31.5) * mm, "mid": v(57.7, -31.6) * mm, "end": v(58.2, -31.21) * mm});
            skLineSegment(sketch, "E24.33.1", {"start": v(55.65, -30.6) * mm, "end": v(57.08, -31.5) * mm});
            skArc(sketch, "E24.33.2", {"start": v(55.65, -30.6) * mm, "mid": v(54.48, -30.4) * mm, "end": v(53.3, -30.3) * mm});
            skArc(sketch, "E24.33.3", {"start": v(53.3, -30.3) * mm, "mid": v(52.9, -30.39) * mm, "end": v(52.6, -30.66) * mm});
            skLineSegment(sketch, "E24.33.4", {"start": v(52.6, -30.66) * mm, "end": v(52.4, -30.99) * mm});
            skLineSegment(sketch, "E24.33.5", {"start": v(52.21, -31.33) * mm, "end": v(52.4, -30.99) * mm});
            skArc(sketch, "E24.33.6", {"start": v(52.21, -31.33) * mm, "mid": v(52.12, -31.72) * mm, "end": v(52.23, -32.12) * mm});
            skArc(sketch, "E24.33.7", {"start": v(53.61, -34.03) * mm, "mid": v(52.89, -33.1) * mm, "end": v(52.23, -32.12) * mm});
            skLineSegment(sketch, "E24.33.8", {"start": v(53.61, -34.03) * mm, "end": v(55.1, -34.85) * mm});
            skArc(sketch, "E24.33.9", {"start": v(55.39, -35.96) * mm, "mid": v(55.5, -35.34) * mm, "end": v(55.1, -34.85) * mm});
            skArc(sketch, "E24.34.0", {"start": v(60.58, -24.1) * mm, "mid": v(61.21, -24.12) * mm, "end": v(61.65, -23.67) * mm});
            skLineSegment(sketch, "E24.34.1", {"start": v(59.04, -23.38) * mm, "end": v(60.58, -24.1) * mm});
            skArc(sketch, "E24.34.2", {"start": v(59.04, -23.38) * mm, "mid": v(57.86, -23.33) * mm, "end": v(56.69, -23.38) * mm});
            skArc(sketch, "E24.34.3", {"start": v(56.69, -23.38) * mm, "mid": v(56.3, -23.52) * mm, "end": v(56.03, -23.83) * mm});
            skLineSegment(sketch, "E24.34.4", {"start": v(56.03, -23.83) * mm, "end": v(55.87, -24.18) * mm});
            skLineSegment(sketch, "E24.34.5", {"start": v(55.73, -24.53) * mm, "end": v(55.87, -24.18) * mm});
            skArc(sketch, "E24.34.6", {"start": v(55.73, -24.53) * mm, "mid": v(55.68, -24.94) * mm, "end": v(55.85, -25.32) * mm});
            skArc(sketch, "E24.34.7", {"start": v(57.46, -27.04) * mm, "mid": v(56.62, -26.2) * mm, "end": v(55.85, -25.32) * mm});
            skLineSegment(sketch, "E24.34.8", {"start": v(57.46, -27.04) * mm, "end": v(59.04, -27.66) * mm});
            skArc(sketch, "E24.34.9", {"start": v(59.46, -28.74) * mm, "mid": v(59.48, -28.1) * mm, "end": v(59.04, -27.66) * mm});
            skArc(sketch, "E24.35.0", {"start": v(63.12, -16.32) * mm, "mid": v(63.75, -16.26) * mm, "end": v(64.13, -15.76) * mm});
            skLineSegment(sketch, "E24.35.1", {"start": v(61.5, -15.8) * mm, "end": v(63.12, -16.32) * mm});
            skArc(sketch, "E24.35.2", {"start": v(61.5, -15.8) * mm, "mid": v(60.33, -15.9) * mm, "end": v(59.17, -16.1) * mm});
            skArc(sketch, "E24.35.3", {"start": v(59.17, -16.1) * mm, "mid": v(58.8, -16.27) * mm, "end": v(58.58, -16.62) * mm});
            skLineSegment(sketch, "E24.35.4", {"start": v(58.58, -16.62) * mm, "end": v(58.46, -16.98) * mm});
            skLineSegment(sketch, "E24.35.5", {"start": v(58.36, -17.36) * mm, "end": v(58.46, -16.98) * mm});
            skArc(sketch, "E24.35.6", {"start": v(58.36, -17.36) * mm, "mid": v(58.37, -17.77) * mm, "end": v(58.58, -18.12) * mm});
            skArc(sketch, "E24.35.7", {"start": v(60.4, -19.62) * mm, "mid": v(59.46, -18.9) * mm, "end": v(58.58, -18.12) * mm});
            skLineSegment(sketch, "E24.35.8", {"start": v(60.4, -19.62) * mm, "end": v(62.04, -20.05) * mm});
            skArc(sketch, "E24.35.9", {"start": v(62.6, -21.06) * mm, "mid": v(62.54, -20.43) * mm, "end": v(62.04, -20.05) * mm});
            skArc(sketch, "E24.36.0", {"start": v(64.67, -8.28) * mm, "mid": v(65.29, -8.14) * mm, "end": v(65.6, -7.6) * mm});
            skLineSegment(sketch, "E24.36.1", {"start": v(63, -7.96) * mm, "end": v(64.67, -8.28) * mm});
            skArc(sketch, "E24.36.2", {"start": v(63, -7.96) * mm, "mid": v(61.85, -8.21) * mm, "end": v(60.72, -8.55) * mm});
            skArc(sketch, "E24.36.3", {"start": v(60.72, -8.55) * mm, "mid": v(60.38, -8.78) * mm, "end": v(60.2, -9.15) * mm});
            skLineSegment(sketch, "E24.36.4", {"start": v(60.2, -9.15) * mm, "end": v(60.13, -9.52) * mm});
            skLineSegment(sketch, "E24.36.5", {"start": v(60.08, -9.9) * mm, "end": v(60.13, -9.52) * mm});
            skArc(sketch, "E24.36.6", {"start": v(60.08, -9.9) * mm, "mid": v(60.14, -10.31) * mm, "end": v(60.39, -10.63) * mm});
            skArc(sketch, "E24.36.7", {"start": v(62.38, -11.9) * mm, "mid": v(61.36, -11.3) * mm, "end": v(60.39, -10.63) * mm});
            skLineSegment(sketch, "E24.36.8", {"start": v(62.38, -11.9) * mm, "end": v(64.06, -12.11) * mm});
            skArc(sketch, "E24.36.9", {"start": v(64.74, -13.05) * mm, "mid": v(64.6, -12.43) * mm, "end": v(64.06, -12.11) * mm});
            skArc(sketch, "E24.37.0", {"start": v(65.2, -0.1) * mm, "mid": v(65.8, 0.1) * mm, "end": v(66.04, 0.69) * mm});
            skLineSegment(sketch, "E24.37.1", {"start": v(63.5, 0) * mm, "end": v(65.2, -0.1) * mm});
            skArc(sketch, "E24.37.2", {"start": v(63.5, 0) * mm, "mid": v(62.39, -0.4) * mm, "end": v(61.31, -0.87) * mm});
            skArc(sketch, "E24.37.3", {"start": v(61.31, -0.87) * mm, "mid": v(61, -1.14) * mm, "end": v(60.87, -1.53) * mm});
            skLineSegment(sketch, "E24.37.4", {"start": v(60.87, -1.53) * mm, "end": v(60.85, -1.91) * mm});
            skLineSegment(sketch, "E24.37.5", {"start": v(60.85, -2.3) * mm, "end": v(60.85, -1.91) * mm});
            skArc(sketch, "E24.37.6", {"start": v(60.85, -2.3) * mm, "mid": v(60.95, -2.7) * mm, "end": v(61.25, -2.98) * mm});
            skArc(sketch, "E24.37.7", {"start": v(63.37, -3.99) * mm, "mid": v(62.3, -3.52) * mm, "end": v(61.25, -2.98) * mm});
            skLineSegment(sketch, "E24.37.8", {"start": v(63.37, -3.99) * mm, "end": v(65.08, -3.99) * mm});
            skArc(sketch, "E24.37.9", {"start": v(65.86, -4.83) * mm, "mid": v(65.65, -4.24) * mm, "end": v(65.08, -3.99) * mm});
            skArc(sketch, "E24.38.0", {"start": v(64.7, 8.07) * mm, "mid": v(65.26, 8.35) * mm, "end": v(65.43, 8.96) * mm});
            skLineSegment(sketch, "E24.38.1", {"start": v(63, 7.96) * mm, "end": v(64.7, 8.07) * mm});
            skArc(sketch, "E24.38.2", {"start": v(63, 7.96) * mm, "mid": v(61.95, 7.43) * mm, "end": v(60.94, 6.82) * mm});
            skArc(sketch, "E24.38.3", {"start": v(60.94, 6.82) * mm, "mid": v(60.66, 6.51) * mm, "end": v(60.58, 6.11) * mm});
            skLineSegment(sketch, "E24.38.4", {"start": v(60.58, 6.11) * mm, "end": v(60.6, 5.73) * mm});
            skLineSegment(sketch, "E24.38.5", {"start": v(60.65, 5.35) * mm, "end": v(60.6, 5.73) * mm});
            skArc(sketch, "E24.38.6", {"start": v(60.65, 5.35) * mm, "mid": v(60.81, 4.97) * mm, "end": v(61.14, 4.72) * mm});
            skArc(sketch, "E24.38.7", {"start": v(63.37, 3.99) * mm, "mid": v(62.24, 4.31) * mm, "end": v(61.14, 4.72) * mm});
            skLineSegment(sketch, "E24.38.8", {"start": v(63.37, 3.99) * mm, "end": v(65.06, 4.2) * mm});
            skArc(sketch, "E24.38.9", {"start": v(65.95, 3.46) * mm, "mid": v(65.67, 4.02) * mm, "end": v(65.06, 4.2) * mm});
            skArc(sketch, "E24.39.0", {"start": v(63.18, 16.11) * mm, "mid": v(63.7, 16.47) * mm, "end": v(63.8, 17.09) * mm});
            skLineSegment(sketch, "E24.39.1", {"start": v(61.5, 15.8) * mm, "end": v(63.18, 16.11) * mm});
            skArc(sketch, "E24.39.2", {"start": v(61.5, 15.8) * mm, "mid": v(60.53, 15.13) * mm, "end": v(59.6, 14.4) * mm});
            skArc(sketch, "E24.39.3", {"start": v(59.6, 14.4) * mm, "mid": v(59.37, 14.07) * mm, "end": v(59.34, 13.66) * mm});
            skLineSegment(sketch, "E24.39.4", {"start": v(59.34, 13.66) * mm, "end": v(59.41, 13.28) * mm});
            skLineSegment(sketch, "E24.39.5", {"start": v(59.5, 12.9) * mm, "end": v(59.41, 13.28) * mm});
            skArc(sketch, "E24.39.6", {"start": v(59.5, 12.9) * mm, "mid": v(59.7, 12.55) * mm, "end": v(60.06, 12.34) * mm});
            skArc(sketch, "E24.39.7", {"start": v(62.38, 11.9) * mm, "mid": v(61.21, 12.08) * mm, "end": v(60.06, 12.34) * mm});
            skLineSegment(sketch, "E24.39.8", {"start": v(62.38, 11.9) * mm, "end": v(64.02, 12.32) * mm});
            skArc(sketch, "E24.39.9", {"start": v(65, 11.7) * mm, "mid": v(64.65, 12.22) * mm, "end": v(64.02, 12.32) * mm});
            skArc(sketch, "E24.40.0", {"start": v(60.66, 23.9) * mm, "mid": v(61.13, 24.32) * mm, "end": v(61.15, 24.95) * mm});
            skLineSegment(sketch, "E24.40.1", {"start": v(59.04, 23.38) * mm, "end": v(60.66, 23.9) * mm});
            skArc(sketch, "E24.40.2", {"start": v(59.04, 23.38) * mm, "mid": v(58.15, 22.6) * mm, "end": v(57.33, 21.76) * mm});
            skArc(sketch, "E24.40.3", {"start": v(57.33, 21.76) * mm, "mid": v(57.14, 21.4) * mm, "end": v(57.16, 20.99) * mm});
            skLineSegment(sketch, "E24.40.4", {"start": v(57.16, 20.99) * mm, "end": v(57.28, 20.62) * mm});
            skLineSegment(sketch, "E24.40.5", {"start": v(57.42, 20.26) * mm, "end": v(57.28, 20.62) * mm});
            skArc(sketch, "E24.40.6", {"start": v(57.42, 20.26) * mm, "mid": v(57.66, 19.93) * mm, "end": v(58.04, 19.77) * mm});
            skArc(sketch, "E24.40.7", {"start": v(60.4, 19.62) * mm, "mid": v(59.21, 19.65) * mm, "end": v(58.04, 19.77) * mm});
            skLineSegment(sketch, "E24.40.8", {"start": v(60.4, 19.62) * mm, "end": v(61.98, 20.25) * mm});
            skArc(sketch, "E24.40.9", {"start": v(63.02, 19.75) * mm, "mid": v(62.6, 20.23) * mm, "end": v(61.98, 20.25) * mm});
            skArc(sketch, "E24.41.0", {"start": v(57.19, 31.32) * mm, "mid": v(57.6, 31.79) * mm, "end": v(57.54, 32.42) * mm});
            skLineSegment(sketch, "E24.41.1", {"start": v(55.65, 30.6) * mm, "end": v(57.19, 31.32) * mm});
            skArc(sketch, "E24.41.2", {"start": v(55.65, 30.6) * mm, "mid": v(54.86, 29.71) * mm, "end": v(54.15, 28.77) * mm});
            skArc(sketch, "E24.41.3", {"start": v(54.15, 28.77) * mm, "mid": v(54, 28.39) * mm, "end": v(54.08, 27.98) * mm});
            skLineSegment(sketch, "E24.41.4", {"start": v(54.08, 27.98) * mm, "end": v(54.24, 27.64) * mm});
            skLineSegment(sketch, "E24.41.5", {"start": v(54.43, 27.3) * mm, "end": v(54.24, 27.64) * mm});
            skArc(sketch, "E24.41.6", {"start": v(54.43, 27.3) * mm, "mid": v(54.71, 27) * mm, "end": v(55.1, 26.9) * mm});
            skArc(sketch, "E24.41.7", {"start": v(57.46, 27.04) * mm, "mid": v(56.28, 26.92) * mm, "end": v(55.1, 26.9) * mm});
            skLineSegment(sketch, "E24.41.8", {"start": v(57.46, 27.04) * mm, "end": v(58.95, 27.86) * mm});
            skArc(sketch, "E24.41.9", {"start": v(60.04, 27.5) * mm, "mid": v(59.58, 27.91) * mm, "end": v(58.95, 27.86) * mm});
            skArc(sketch, "E24.42.0", {"start": v(52.81, 38.24) * mm, "mid": v(53.16, 38.76) * mm, "end": v(53.02, 39.37) * mm});
            skLineSegment(sketch, "E24.42.1", {"start": v(51.37, 37.32) * mm, "end": v(52.81, 38.24) * mm});
            skArc(sketch, "E24.42.2", {"start": v(51.37, 37.32) * mm, "mid": v(50.7, 36.35) * mm, "end": v(50.11, 35.33) * mm});
            skArc(sketch, "E24.42.3", {"start": v(50.11, 35.33) * mm, "mid": v(50.02, 34.93) * mm, "end": v(50.14, 34.54) * mm});
            skLineSegment(sketch, "E24.42.4", {"start": v(50.14, 34.54) * mm, "end": v(50.35, 34.22) * mm});
            skLineSegment(sketch, "E24.42.5", {"start": v(50.58, 33.9) * mm, "end": v(50.35, 34.22) * mm});
            skArc(sketch, "E24.42.6", {"start": v(50.58, 33.9) * mm, "mid": v(50.9, 33.65) * mm, "end": v(51.3, 33.59) * mm});
            skArc(sketch, "E24.42.7", {"start": v(53.61, 34.03) * mm, "mid": v(52.47, 33.76) * mm, "end": v(51.3, 33.59) * mm});
            skLineSegment(sketch, "E24.42.8", {"start": v(53.61, 34.03) * mm, "end": v(55, 35.03) * mm});
            skArc(sketch, "E24.42.9", {"start": v(56.12, 34.8) * mm, "mid": v(55.6, 35.16) * mm, "end": v(55, 35.03) * mm});
            skArc(sketch, "E24.43.0", {"start": v(47.6, 44.55) * mm, "mid": v(47.89, 45.12) * mm, "end": v(47.67, 45.7) * mm});
            skLineSegment(sketch, "E24.43.1", {"start": v(46.29, 43.47) * mm, "end": v(47.6, 44.55) * mm});
            skArc(sketch, "E24.43.2", {"start": v(46.29, 43.47) * mm, "mid": v(45.75, 42.42) * mm, "end": v(45.3, 41.34) * mm});
            skArc(sketch, "E24.43.3", {"start": v(45.3, 41.34) * mm, "mid": v(45.25, 40.93) * mm, "end": v(45.42, 40.55) * mm});
            skLineSegment(sketch, "E24.43.4", {"start": v(45.42, 40.55) * mm, "end": v(45.66, 40.26) * mm});
            skLineSegment(sketch, "E24.43.5", {"start": v(45.93, 39.98) * mm, "end": v(45.66, 40.26) * mm});
            skArc(sketch, "E24.43.6", {"start": v(45.93, 39.98) * mm, "mid": v(46.28, 39.76) * mm, "end": v(46.69, 39.75) * mm});
            skArc(sketch, "E24.43.7", {"start": v(48.93, 40.48) * mm, "mid": v(47.82, 40.07) * mm, "end": v(46.69, 39.75) * mm});
            skLineSegment(sketch, "E24.43.8", {"start": v(48.93, 40.48) * mm, "end": v(50.17, 41.64) * mm});
            skArc(sketch, "E24.43.9", {"start": v(51.32, 41.56) * mm, "mid": v(50.76, 41.85) * mm, "end": v(50.17, 41.64) * mm});
            skArc(sketch, "E24.44.0", {"start": v(41.64, 50.17) * mm, "mid": v(41.85, 50.76) * mm, "end": v(41.56, 51.32) * mm});
            skLineSegment(sketch, "E24.44.1", {"start": v(40.48, 48.93) * mm, "end": v(41.64, 50.17) * mm});
            skArc(sketch, "E24.44.2", {"start": v(40.48, 48.93) * mm, "mid": v(40.07, 47.82) * mm, "end": v(39.75, 46.69) * mm});
            skArc(sketch, "E24.44.3", {"start": v(39.75, 46.69) * mm, "mid": v(39.76, 46.28) * mm, "end": v(39.98, 45.93) * mm});
            skLineSegment(sketch, "E24.44.4", {"start": v(39.98, 45.93) * mm, "end": v(40.26, 45.66) * mm});
            skLineSegment(sketch, "E24.44.5", {"start": v(40.55, 45.42) * mm, "end": v(40.26, 45.66) * mm});
            skArc(sketch, "E24.44.6", {"start": v(40.55, 45.42) * mm, "mid": v(40.93, 45.25) * mm, "end": v(41.34, 45.3) * mm});
            skArc(sketch, "E24.44.7", {"start": v(43.47, 46.29) * mm, "mid": v(42.42, 45.75) * mm, "end": v(41.34, 45.3) * mm});
            skLineSegment(sketch, "E24.44.8", {"start": v(43.47, 46.29) * mm, "end": v(44.55, 47.6) * mm});
            skArc(sketch, "E24.44.9", {"start": v(45.7, 47.67) * mm, "mid": v(45.12, 47.89) * mm, "end": v(44.55, 47.6) * mm});
            skArc(sketch, "E24.45.0", {"start": v(35.03, 55) * mm, "mid": v(35.16, 55.6) * mm, "end": v(34.8, 56.12) * mm});
            skLineSegment(sketch, "E24.45.1", {"start": v(34.03, 53.61) * mm, "end": v(35.03, 55) * mm});
            skArc(sketch, "E24.45.2", {"start": v(34.03, 53.61) * mm, "mid": v(33.76, 52.47) * mm, "end": v(33.59, 51.3) * mm});
            skArc(sketch, "E24.45.3", {"start": v(33.59, 51.3) * mm, "mid": v(33.65, 50.9) * mm, "end": v(33.9, 50.58) * mm});
            skLineSegment(sketch, "E24.45.4", {"start": v(33.9, 50.58) * mm, "end": v(34.22, 50.35) * mm});
            skLineSegment(sketch, "E24.45.5", {"start": v(34.54, 50.14) * mm, "end": v(34.22, 50.35) * mm});
            skArc(sketch, "E24.45.6", {"start": v(34.54, 50.14) * mm, "mid": v(34.93, 50.02) * mm, "end": v(35.33, 50.11) * mm});
            skArc(sketch, "E24.45.7", {"start": v(37.32, 51.37) * mm, "mid": v(36.35, 50.7) * mm, "end": v(35.33, 50.11) * mm});
            skLineSegment(sketch, "E24.45.8", {"start": v(37.32, 51.37) * mm, "end": v(38.24, 52.81) * mm});
            skArc(sketch, "E24.45.9", {"start": v(39.37, 53.02) * mm, "mid": v(38.76, 53.16) * mm, "end": v(38.24, 52.81) * mm});
            skArc(sketch, "E24.46.0", {"start": v(27.86, 58.95) * mm, "mid": v(27.91, 59.58) * mm, "end": v(27.5, 60.04) * mm});
            skLineSegment(sketch, "E24.46.1", {"start": v(27.04, 57.46) * mm, "end": v(27.86, 58.95) * mm});
            skArc(sketch, "E24.46.2", {"start": v(27.04, 57.46) * mm, "mid": v(26.92, 56.28) * mm, "end": v(26.9, 55.1) * mm});
            skArc(sketch, "E24.46.3", {"start": v(26.9, 55.1) * mm, "mid": v(27, 54.71) * mm, "end": v(27.3, 54.43) * mm});
            skLineSegment(sketch, "E24.46.4", {"start": v(27.3, 54.43) * mm, "end": v(27.64, 54.24) * mm});
            skLineSegment(sketch, "E24.46.5", {"start": v(27.98, 54.08) * mm, "end": v(27.64, 54.24) * mm});
            skArc(sketch, "E24.46.6", {"start": v(27.98, 54.08) * mm, "mid": v(28.39, 54) * mm, "end": v(28.77, 54.15) * mm});
            skArc(sketch, "E24.46.7", {"start": v(30.6, 55.65) * mm, "mid": v(29.71, 54.86) * mm, "end": v(28.77, 54.15) * mm});
            skLineSegment(sketch, "E24.46.8", {"start": v(30.6, 55.65) * mm, "end": v(31.32, 57.19) * mm});
            skArc(sketch, "E24.46.9", {"start": v(32.42, 57.54) * mm, "mid": v(31.79, 57.6) * mm, "end": v(31.32, 57.19) * mm});
            skArc(sketch, "E24.47.0", {"start": v(20.25, 61.98) * mm, "mid": v(20.23, 62.6) * mm, "end": v(19.75, 63.02) * mm});
            skLineSegment(sketch, "E24.47.1", {"start": v(19.62, 60.4) * mm, "end": v(20.25, 61.98) * mm});
            skArc(sketch, "E24.47.2", {"start": v(19.62, 60.4) * mm, "mid": v(19.65, 59.21) * mm, "end": v(19.77, 58.04) * mm});
            skArc(sketch, "E24.47.3", {"start": v(19.77, 58.04) * mm, "mid": v(19.93, 57.66) * mm, "end": v(20.26, 57.42) * mm});
            skLineSegment(sketch, "E24.47.4", {"start": v(20.26, 57.42) * mm, "end": v(20.62, 57.28) * mm});
            skLineSegment(sketch, "E24.47.5", {"start": v(20.99, 57.16) * mm, "end": v(20.62, 57.28) * mm});
            skArc(sketch, "E24.47.6", {"start": v(20.99, 57.16) * mm, "mid": v(21.4, 57.14) * mm, "end": v(21.76, 57.33) * mm});
            skArc(sketch, "E24.47.7", {"start": v(23.38, 59.04) * mm, "mid": v(22.6, 58.15) * mm, "end": v(21.76, 57.33) * mm});
            skLineSegment(sketch, "E24.47.8", {"start": v(23.38, 59.04) * mm, "end": v(23.9, 60.66) * mm});
            skArc(sketch, "E24.47.9", {"start": v(24.95, 61.15) * mm, "mid": v(24.32, 61.13) * mm, "end": v(23.9, 60.66) * mm});
            skArc(sketch, "E24.48.0", {"start": v(12.32, 64.02) * mm, "mid": v(12.22, 64.65) * mm, "end": v(11.7, 65) * mm});
            skLineSegment(sketch, "E24.48.1", {"start": v(11.9, 62.38) * mm, "end": v(12.32, 64.02) * mm});
            skArc(sketch, "E24.48.2", {"start": v(11.9, 62.38) * mm, "mid": v(12.08, 61.21) * mm, "end": v(12.34, 60.06) * mm});
            skArc(sketch, "E24.48.3", {"start": v(12.34, 60.06) * mm, "mid": v(12.55, 59.7) * mm, "end": v(12.9, 59.5) * mm});
            skLineSegment(sketch, "E24.48.4", {"start": v(12.9, 59.5) * mm, "end": v(13.28, 59.41) * mm});
            skLineSegment(sketch, "E24.48.5", {"start": v(13.66, 59.34) * mm, "end": v(13.28, 59.41) * mm});
            skArc(sketch, "E24.48.6", {"start": v(13.66, 59.34) * mm, "mid": v(14.07, 59.37) * mm, "end": v(14.4, 59.6) * mm});
            skArc(sketch, "E24.48.7", {"start": v(15.8, 61.5) * mm, "mid": v(15.13, 60.53) * mm, "end": v(14.4, 59.6) * mm});
            skLineSegment(sketch, "E24.48.8", {"start": v(15.8, 61.5) * mm, "end": v(16.11, 63.18) * mm});
            skArc(sketch, "E24.48.9", {"start": v(17.09, 63.8) * mm, "mid": v(16.47, 63.7) * mm, "end": v(16.11, 63.18) * mm});
            skArc(sketch, "E24.49.0", {"start": v(4.2, 65.06) * mm, "mid": v(4.02, 65.67) * mm, "end": v(3.46, 65.95) * mm});
            skLineSegment(sketch, "E24.49.1", {"start": v(3.99, 63.37) * mm, "end": v(4.2, 65.06) * mm});
            skArc(sketch, "E24.49.2", {"start": v(3.99, 63.37) * mm, "mid": v(4.31, 62.24) * mm, "end": v(4.72, 61.14) * mm});
            skArc(sketch, "E24.49.3", {"start": v(4.72, 61.14) * mm, "mid": v(4.97, 60.81) * mm, "end": v(5.35, 60.65) * mm});
            skLineSegment(sketch, "E24.49.4", {"start": v(5.35, 60.65) * mm, "end": v(5.73, 60.6) * mm});
            skLineSegment(sketch, "E24.49.5", {"start": v(6.11, 60.58) * mm, "end": v(5.73, 60.6) * mm});
            skArc(sketch, "E24.49.6", {"start": v(6.11, 60.58) * mm, "mid": v(6.51, 60.66) * mm, "end": v(6.82, 60.94) * mm});
            skArc(sketch, "E24.49.7", {"start": v(7.96, 63) * mm, "mid": v(7.43, 61.95) * mm, "end": v(6.82, 60.94) * mm});
            skLineSegment(sketch, "E24.49.8", {"start": v(7.96, 63) * mm, "end": v(8.07, 64.7) * mm});
            skArc(sketch, "E24.49.9", {"start": v(8.96, 65.43) * mm, "mid": v(8.35, 65.26) * mm, "end": v(8.07, 64.7) * mm});
            skArc(sketch, "E25.trimOffspring", {"start": v(-13.05, 64.74) * mm, "mid": v(-14.4, 64.45) * mm, "end": v(-15.76, 64.13) * mm});
            skArc(sketch, "E26.trimOffspring", {"start": v(-21.06, 62.6) * mm, "mid": v(-22.37, 62.14) * mm, "end": v(-23.67, 61.65) * mm});
            skArc(sketch, "E27.trimOffspring", {"start": v(-28.74, 59.46) * mm, "mid": v(-29.98, 58.84) * mm, "end": v(-31.21, 58.2) * mm});
            skArc(sketch, "E28.trimOffspring", {"start": v(-35.96, 55.39) * mm, "mid": v(-37.12, 54.62) * mm, "end": v(-38.26, 53.83) * mm});
            skArc(sketch, "E29.trimOffspring", {"start": v(-42.62, 50.44) * mm, "mid": v(-43.67, 49.54) * mm, "end": v(-44.7, 48.6) * mm});
            skArc(sketch, "E30.trimOffspring", {"start": v(-22.72, 67.4) * mm, "mid": v(3.72, -71.02) * mm, "end": v(15.55, 69.4) * mm});
            skArc(sketch, "E31.trimOffspring", {"start": v(6.66, 70.8) * mm, "mid": v(3.72, 71.02) * mm, "end": v(0.78, 71.12) * mm});
            skArc(sketch, "E32.trimOffspring", {"start": v(3.46, 65.95) * mm, "mid": v(2.07, 66) * mm, "end": v(0.69, 66.04) * mm});
            skArc(sketch, "E33.trimOffspring", {"start": v(11.7, 65) * mm, "mid": v(10.33, 65.23) * mm, "end": v(8.96, 65.43) * mm});
            skArc(sketch, "E34.trimOffspring", {"start": v(19.75, 63.02) * mm, "mid": v(18.42, 63.42) * mm, "end": v(17.09, 63.8) * mm});
            skArc(sketch, "E35.trimOffspring", {"start": v(27.5, 60.04) * mm, "mid": v(26.23, 60.6) * mm, "end": v(24.95, 61.15) * mm});
            skArc(sketch, "E36.trimOffspring", {"start": v(34.8, 56.12) * mm, "mid": v(33.62, 56.84) * mm, "end": v(32.42, 57.54) * mm});
            skArc(sketch, "E37.trimOffspring", {"start": v(41.56, 51.32) * mm, "mid": v(40.48, 52.18) * mm, "end": v(39.37, 53.02) * mm});
            skArc(sketch, "E38.trimOffspring", {"start": v(47.67, 45.7) * mm, "mid": v(46.7, 46.7) * mm, "end": v(45.7, 47.67) * mm});
            skArc(sketch, "E39.trimOffspring", {"start": v(-48.6, 44.7) * mm, "mid": v(-49.54, 43.67) * mm, "end": v(-50.44, 42.62) * mm});
            skArc(sketch, "E40.trimOffspring", {"start": v(-53.83, 38.26) * mm, "mid": v(-54.62, 37.12) * mm, "end": v(-55.39, 35.96) * mm});
            skArc(sketch, "E41.trimOffspring", {"start": v(53.02, 39.37) * mm, "mid": v(52.18, 40.48) * mm, "end": v(51.32, 41.56) * mm});
            skArc(sketch, "E42.trimOffspring", {"start": v(57.54, 32.42) * mm, "mid": v(56.84, 33.62) * mm, "end": v(56.12, 34.8) * mm});
            skArc(sketch, "E43.trimOffspring", {"start": v(-58.2, 31.21) * mm, "mid": v(-58.84, 29.98) * mm, "end": v(-59.46, 28.74) * mm});
            skArc(sketch, "E44.trimOffspring", {"start": v(-61.65, 23.67) * mm, "mid": v(-62.14, 22.37) * mm, "end": v(-62.6, 21.06) * mm});
            skArc(sketch, "E45.trimOffspring", {"start": v(-64.13, 15.76) * mm, "mid": v(-64.45, 14.4) * mm, "end": v(-64.74, 13.05) * mm});
            skArc(sketch, "E46.trimOffspring", {"start": v(-65.6, 7.6) * mm, "mid": v(-65.75, 6.21) * mm, "end": v(-65.86, 4.83) * mm});
            skArc(sketch, "E47.trimOffspring", {"start": v(-66.04, -0.69) * mm, "mid": v(-66, -2.07) * mm, "end": v(-65.95, -3.46) * mm});
            skArc(sketch, "E48.trimOffspring", {"start": v(-65.43, -8.96) * mm, "mid": v(-65.23, -10.33) * mm, "end": v(-65, -11.7) * mm});
            skArc(sketch, "E49.trimOffspring", {"start": v(-63.8, -17.09) * mm, "mid": v(-63.42, -18.42) * mm, "end": v(-63.02, -19.75) * mm});
            skArc(sketch, "E50.trimOffspring", {"start": v(-61.15, -24.95) * mm, "mid": v(-60.6, -26.23) * mm, "end": v(-60.04, -27.5) * mm});
            skArc(sketch, "E51.trimOffspring", {"start": v(-57.54, -32.42) * mm, "mid": v(-56.84, -33.62) * mm, "end": v(-56.12, -34.8) * mm});
            skArc(sketch, "E52.trimOffspring", {"start": v(-53.02, -39.37) * mm, "mid": v(-52.18, -40.48) * mm, "end": v(-51.32, -41.56) * mm});
            skArc(sketch, "E53.trimOffspring", {"start": v(-47.67, -45.7) * mm, "mid": v(-46.7, -46.7) * mm, "end": v(-45.7, -47.67) * mm});
            skArc(sketch, "E54.trimOffspring", {"start": v(-41.56, -51.32) * mm, "mid": v(-40.48, -52.18) * mm, "end": v(-39.37, -53.02) * mm});
            skArc(sketch, "E55.trimOffspring", {"start": v(-34.8, -56.12) * mm, "mid": v(-33.62, -56.84) * mm, "end": v(-32.42, -57.54) * mm});
            skArc(sketch, "E56.trimOffspring", {"start": v(-27.5, -60.04) * mm, "mid": v(-26.23, -60.6) * mm, "end": v(-24.95, -61.15) * mm});
            skArc(sketch, "E57.trimOffspring", {"start": v(-19.75, -63.02) * mm, "mid": v(-18.42, -63.42) * mm, "end": v(-17.09, -63.8) * mm});
            skArc(sketch, "E58.trimOffspring", {"start": v(-11.7, -65) * mm, "mid": v(-10.33, -65.23) * mm, "end": v(-8.96, -65.43) * mm});
            skArc(sketch, "E59.trimOffspring", {"start": v(-3.46, -65.95) * mm, "mid": v(-2.07, -66) * mm, "end": v(-0.69, -66.04) * mm});
            skArc(sketch, "E60.trimOffspring", {"start": v(4.83, -65.86) * mm, "mid": v(6.21, -65.75) * mm, "end": v(7.6, -65.6) * mm});
            skArc(sketch, "E61.trimOffspring", {"start": v(13.05, -64.74) * mm, "mid": v(14.4, -64.45) * mm, "end": v(15.76, -64.13) * mm});
            skArc(sketch, "E62.trimOffspring", {"start": v(21.06, -62.6) * mm, "mid": v(22.37, -62.14) * mm, "end": v(23.67, -61.65) * mm});
            skArc(sketch, "E63.trimOffspring", {"start": v(28.74, -59.46) * mm, "mid": v(29.98, -58.84) * mm, "end": v(31.21, -58.2) * mm});
            skArc(sketch, "E64.trimOffspring", {"start": v(35.96, -55.39) * mm, "mid": v(37.12, -54.62) * mm, "end": v(38.26, -53.83) * mm});
            skArc(sketch, "E65.trimOffspring", {"start": v(48.6, -44.7) * mm, "mid": v(49.54, -43.67) * mm, "end": v(50.44, -42.62) * mm});
            skArc(sketch, "E66.trimOffspring", {"start": v(42.62, -50.44) * mm, "mid": v(43.67, -49.54) * mm, "end": v(44.7, -48.6) * mm});
            skArc(sketch, "E67.trimOffspring", {"start": v(53.83, -38.26) * mm, "mid": v(54.62, -37.12) * mm, "end": v(55.39, -35.96) * mm});
            skArc(sketch, "E68.trimOffspring", {"start": v(58.2, -31.21) * mm, "mid": v(58.84, -29.98) * mm, "end": v(59.46, -28.74) * mm});
            skArc(sketch, "E69.trimOffspring", {"start": v(61.65, -23.67) * mm, "mid": v(62.14, -22.37) * mm, "end": v(62.6, -21.06) * mm});
            skArc(sketch, "E70.trimOffspring", {"start": v(64.13, -15.76) * mm, "mid": v(64.45, -14.4) * mm, "end": v(64.74, -13.05) * mm});
            skArc(sketch, "E71.trimOffspring", {"start": v(65.6, -7.6) * mm, "mid": v(65.75, -6.21) * mm, "end": v(65.86, -4.83) * mm});
            skArc(sketch, "E72.trimOffspring", {"start": v(66.04, 0.69) * mm, "mid": v(66, 2.07) * mm, "end": v(65.95, 3.46) * mm});
            skArc(sketch, "E73.trimOffspring", {"start": v(65.43, 8.96) * mm, "mid": v(65.23, 10.33) * mm, "end": v(65, 11.7) * mm});
            skArc(sketch, "E74.trimOffspring", {"start": v(63.8, 17.09) * mm, "mid": v(63.42, 18.42) * mm, "end": v(63.02, 19.75) * mm});
            skArc(sketch, "E75.trimOffspring", {"start": v(61.15, 24.95) * mm, "mid": v(60.6, 26.23) * mm, "end": v(60.04, 27.5) * mm});
            skSolve(sketch);
        }
        {
            var Q0;
            Q0 = qSketchRegion(id + "F0", true);
            extrude(context, id + "F1", {"entities" : qUnion([Q0]), "depth" : 127 * mm});
        }
    });
